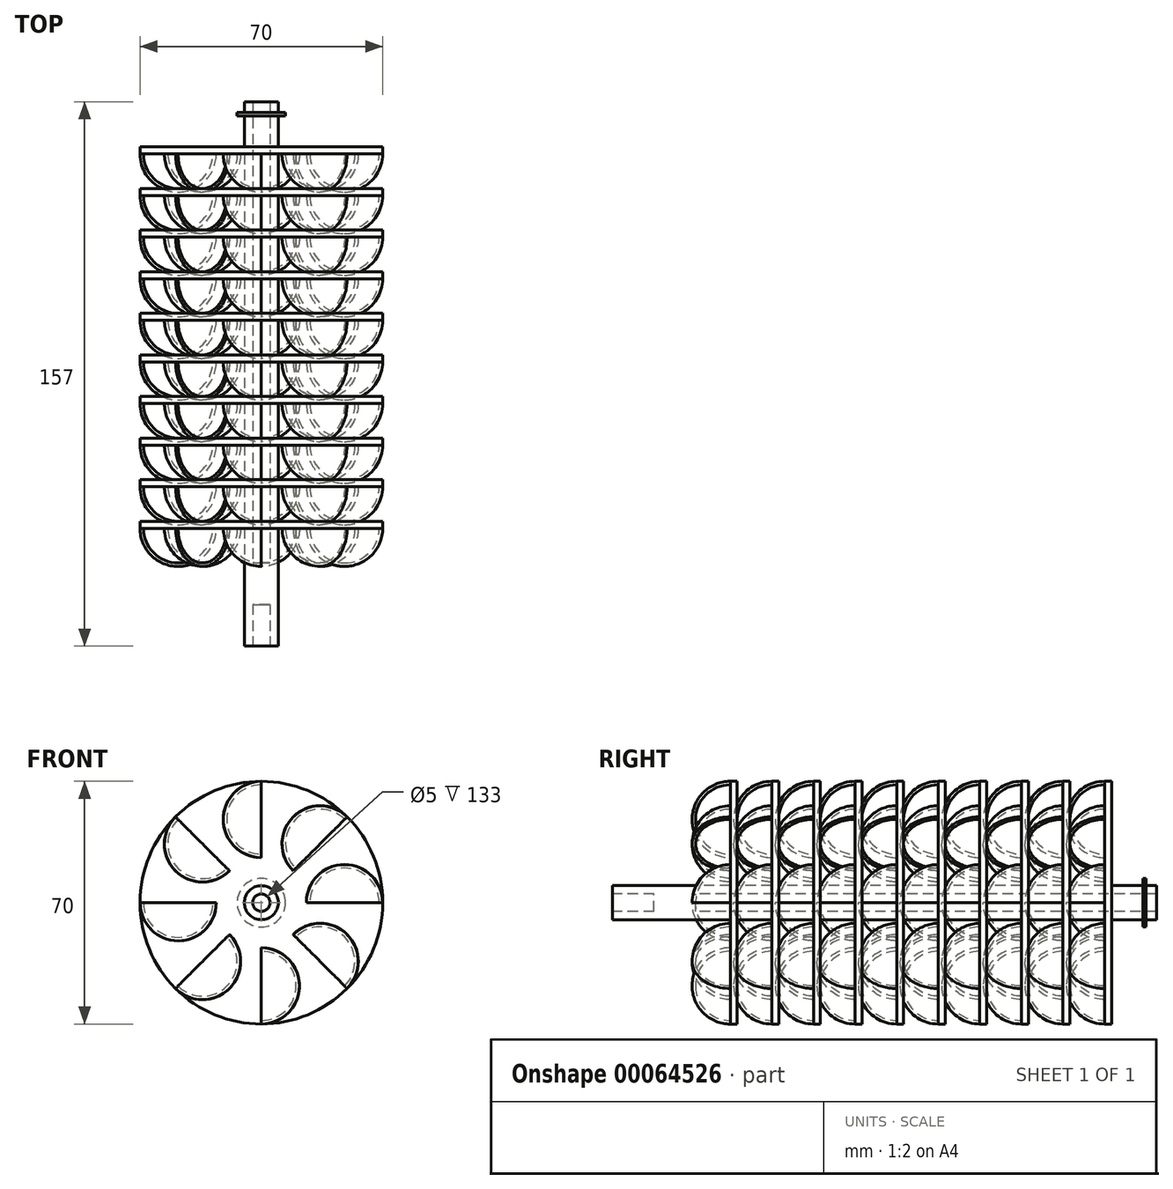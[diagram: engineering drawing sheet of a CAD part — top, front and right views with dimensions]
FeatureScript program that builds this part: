
annotation { "Feature Type Name" : "Feature", "Feature Type Description" : "" }
export const myFeature = defineFeature(function(context is Context, id is Id, definition is map)
    precondition{}
    {
        {
            var Q0;
            Q0=qCreatedBy(makeId("Right.planeOp"),FACE);
            var sketch = newSketch(context, id + "F0", { "sketchPlane" : qUnion([Q0])});
            skArc(sketch, "E0", {"start": v(0, 10) * mm, "mid": v(-7.07, 7.07) * mm, "end": v(-10, 0) * mm});
            skLineSegment(sketch, "E1", {"start": v(-10, 0) * mm, "end": v(0, 0) * mm});
            skLineSegment(sketch, "E2", {"start": v(0, 10) * mm, "end": v(0, 0) * mm});
            skArc(sketch, "E3", {"start": v(0, 11) * mm, "mid": v(-7.78, 7.78) * mm, "end": v(-11, 0) * mm});
            skLineSegment(sketch, "E4", {"start": v(0, 10) * mm, "end": v(0, 11) * mm});
            skLineSegment(sketch, "E5", {"start": v(-11, 0) * mm, "end": v(-10, 0) * mm});
            skSolve(sketch);
        }
        {
            var Q0;
            Q0=makeQuery(id+"F0.imprint","IMPRINT",FACE,{"disambiguationData":[TD([[makeQuery(id+"F0.imprint","IMPRINT",EDGE,{"derivedFrom":sQuery(id+"F0.wireOp",EDGE,"E0")}),-1.0]])]});
            var Q1;
            Q1=sQuery(id+"F0.wireOp",EDGE,"E0");
            var Q2;
            Q2=sQuery(id+"F0.wireOp",EDGE,"E1");
            revolve(context, id + "F1", {"entities" : qUnion([Q0]), "surfaceEntities" : qUnion([Q1]), "axis" : qUnion([Q2]), "revolveType" : RevolveType.TWO_DIRECTIONS, "angle" : 90 * degree, "angleBack" : 270 * degree});
        }
        {
            var Q0;
            Q0=makeQuery(id+"F1.opRevolve","SWEPT_BODY",BODY,{"disambiguationData":[OSD([sQuery(id+"F0.wireOp",EDGE,"E0"),sQuery(id+"F0.wireOp",EDGE,"E3"),sQuery(id+"F0.wireOp",EDGE,"E4"),sQuery(id+"F0.wireOp",EDGE,"E5")])]});
            transform(context, id + "F2", {"entities" : qUnion([Q0]), "transformType" : TransformType.TRANSLATION_3D, "dx" : 24 * mm, "dy" : 0 * mm, "dz" : 0 * mm, "makeCopy" : false});
        }
        {
            var Q0;
            Q0=qCreatedBy(makeId("Right.planeOp"),FACE);
            var sketch = newSketch(context, id + "F3", { "sketchPlane" : qUnion([Q0])});
            skLineSegment(sketch, "E6", {"start": v(-12, 0) * mm, "end": v(0, 0) * mm});
            skLineSegment(sketch, "E7", {"start": v(0, 0) * mm, "end": v(10, 0) * mm});
            skLineSegment(sketch, "E8", {"start": v(0, 0) * mm, "end": v(0, 35) * mm});
            skLineSegment(sketch, "E9.bottom", {"start": v(-2, 0) * mm, "end": v(0, 0) * mm});
            skLineSegment(sketch, "E9.top", {"start": v(-2, 35) * mm, "end": v(0, 35) * mm});
            skLineSegment(sketch, "E9.right", {"start": v(-2, 0) * mm, "end": v(-2, 35) * mm});
            skLineSegment(sketch, "E10", {"start": v(-24, 4.9) * mm, "end": v(0, 4.9) * mm});
            skLineSegment(sketch, "E11", {"start": v(0, 4.9) * mm, "end": v(10, 4.9) * mm});
            skLineSegment(sketch, "E12", {"start": v(-2, 4.9) * mm, "end": v(-2, 0) * mm});
            skLineSegment(sketch, "E13", {"start": v(0, 4.9) * mm, "end": v(0, 0) * mm});
            skLineSegment(sketch, "E14", {"start": v(22, 0) * mm, "end": v(34, 0) * mm});
            skLineSegment(sketch, "E15", {"start": v(34, 0) * mm, "end": v(46, 0) * mm});
            skLineSegment(sketch, "E16", {"start": v(-12, 0) * mm, "end": v(-24, 0) * mm});
            skLineSegment(sketch, "E17", {"start": v(-24, 0) * mm, "end": v(-36, 0) * mm});
            skLineSegment(sketch, "E18", {"start": v(-36, 0) * mm, "end": v(-48, 0) * mm});
            skLineSegment(sketch, "E19", {"start": v(10, 0) * mm, "end": v(22, 0) * mm});
            skLineSegment(sketch, "E20", {"start": v(46, 0) * mm, "end": v(58, 0) * mm});
            skLineSegment(sketch, "E21", {"start": v(-24, 4.9) * mm, "end": v(-24, 4.9) * mm});
            skLineSegment(sketch, "E22", {"start": v(10, 4.9) * mm, "end": v(22, 4.9) * mm});
            skLineSegment(sketch, "E23", {"start": v(-24, 4.9) * mm, "end": v(-36, 4.9) * mm});
            skLineSegment(sketch, "E24", {"start": v(-36, 0) * mm, "end": v(-36, 4.9) * mm});
            skLineSegment(sketch, "E25", {"start": v(58, 0) * mm, "end": v(73, 0) * mm});
            skLineSegment(sketch, "E26", {"start": v(73, 0) * mm, "end": v(85, 0) * mm});
            skLineSegment(sketch, "E27", {"start": v(-48, 0) * mm, "end": v(-60, 0) * mm});
            skLineSegment(sketch, "E28", {"start": v(-36, 0) * mm, "end": v(-36, 2.5) * mm});
            skLineSegment(sketch, "E29", {"start": v(-36, 2.5) * mm, "end": v(22, 2.5) * mm});
            skLineSegment(sketch, "E30", {"start": v(-36, 0) * mm, "end": v(-38, 0) * mm});
            skLineSegment(sketch, "E31", {"start": v(10, 4.9) * mm, "end": v(10, 0) * mm});
            skLineSegment(sketch, "E32", {"start": v(10, 0) * mm, "end": v(10, 35) * mm});
            skLineSegment(sketch, "E33", {"start": v(10, 35) * mm, "end": v(12, 35) * mm});
            skLineSegment(sketch, "E34", {"start": v(12, 35) * mm, "end": v(12, 0) * mm});
            skLineSegment(sketch, "E35", {"start": v(22, 0) * mm, "end": v(22, 35) * mm});
            skLineSegment(sketch, "E36", {"start": v(22, 35) * mm, "end": v(24, 35) * mm});
            skLineSegment(sketch, "E37", {"start": v(24, 35) * mm, "end": v(24, 0) * mm});
            skLineSegment(sketch, "E38", {"start": v(34, 0) * mm, "end": v(34, 35) * mm});
            skLineSegment(sketch, "E39", {"start": v(34, 35) * mm, "end": v(36, 35) * mm});
            skLineSegment(sketch, "E40", {"start": v(36, 35) * mm, "end": v(36, 0) * mm});
            skLineSegment(sketch, "E41", {"start": v(46, 0) * mm, "end": v(46, 35) * mm});
            skLineSegment(sketch, "E42", {"start": v(46, 35) * mm, "end": v(48, 35) * mm});
            skLineSegment(sketch, "E43", {"start": v(48, 35) * mm, "end": v(48, 0) * mm});
            skLineSegment(sketch, "E44", {"start": v(58, 0) * mm, "end": v(58, 35) * mm});
            skLineSegment(sketch, "E45", {"start": v(58, 35) * mm, "end": v(60, 35) * mm});
            skLineSegment(sketch, "E46", {"start": v(60, 35) * mm, "end": v(60, 0) * mm});
            skLineSegment(sketch, "E47", {"start": v(22, 4.9) * mm, "end": v(34, 4.9) * mm});
            skLineSegment(sketch, "E48", {"start": v(34, 4.9) * mm, "end": v(46, 4.9) * mm});
            skLineSegment(sketch, "E49", {"start": v(46, 4.9) * mm, "end": v(58, 4.9) * mm});
            skLineSegment(sketch, "E50", {"start": v(58, 4.9) * mm, "end": v(73, 4.9) * mm});
            skLineSegment(sketch, "E51", {"start": v(73, 4.9) * mm, "end": v(73, 0) * mm});
            skLineSegment(sketch, "E52", {"start": v(22, 2.5) * mm, "end": v(48, 2.5) * mm});
            skLineSegment(sketch, "E53", {"start": v(48, 2.5) * mm, "end": v(73, 2.5) * mm});
            skLineSegment(sketch, "E54", {"start": v(-12, 0) * mm, "end": v(-12, 35) * mm});
            skLineSegment(sketch, "E55", {"start": v(-12, 35) * mm, "end": v(-14, 35) * mm});
            skLineSegment(sketch, "E56", {"start": v(-14, 35) * mm, "end": v(-14, 0) * mm});
            skLineSegment(sketch, "E57", {"start": v(-24, 0) * mm, "end": v(-24, 35) * mm});
            skLineSegment(sketch, "E58", {"start": v(-24, 35) * mm, "end": v(-26, 35) * mm});
            skLineSegment(sketch, "E59", {"start": v(-26, 35) * mm, "end": v(-26, 0) * mm});
            skLineSegment(sketch, "E60", {"start": v(-36, 0) * mm, "end": v(-36, 35) * mm});
            skLineSegment(sketch, "E61", {"start": v(-36, 35) * mm, "end": v(-38, 35) * mm});
            skLineSegment(sketch, "E62", {"start": v(-38, 35) * mm, "end": v(-38, 0) * mm});
            skLineSegment(sketch, "E63", {"start": v(-48, 0) * mm, "end": v(-48, 35) * mm});
            skLineSegment(sketch, "E64", {"start": v(-48, 35) * mm, "end": v(-50, 35) * mm});
            skLineSegment(sketch, "E65", {"start": v(-50, 35) * mm, "end": v(-50, 0) * mm});
            skLineSegment(sketch, "E66", {"start": v(-36, 4.9) * mm, "end": v(-50, 4.9) * mm});
            skLineSegment(sketch, "E67", {"start": v(-50, 4.9) * mm, "end": v(-60, 4.9) * mm});
            skLineSegment(sketch, "E68", {"start": v(-60, 4.9) * mm, "end": v(-60, 0) * mm});
            skLineSegment(sketch, "E69", {"start": v(-36, 2.5) * mm, "end": v(-60, 2.5) * mm});
            skLineSegment(sketch, "E70", {"start": v(-60, 0) * mm, "end": v(-60, 2.5) * mm});
            skLineSegment(sketch, "E71", {"start": v(-2, 4.9) * mm, "end": v(0, 4.9) * mm});
            skLineSegment(sketch, "E72", {"start": v(0, 0) * mm, "end": v(-2, 0) * mm});
            skLineSegment(sketch, "E73", {"start": v(10, 0) * mm, "end": v(-2, 0) * mm});
            skLineSegment(sketch, "E74", {"start": v(10, 4.9) * mm, "end": v(-2, 4.9) * mm});
            skLineSegment(sketch, "E75", {"start": v(22, 2.5) * mm, "end": v(12, 2.5) * mm});
            skLineSegment(sketch, "E76", {"start": v(-2, 4.9) * mm, "end": v(10, 4.9) * mm});
            skLineSegment(sketch, "E77", {"start": v(-60, 4.9) * mm, "end": v(-72, 4.9) * mm});
            skLineSegment(sketch, "E78", {"start": v(-72, 4.9) * mm, "end": v(-72, 0) * mm});
            skLineSegment(sketch, "E79", {"start": v(-72, 0) * mm, "end": v(-60, 0) * mm});
            skLineSegment(sketch, "E80", {"start": v(-72, 4.9) * mm, "end": v(-84, 4.9) * mm});
            skLineSegment(sketch, "E81", {"start": v(-84, 4.9) * mm, "end": v(-84, 0) * mm});
            skLineSegment(sketch, "E82", {"start": v(-84, 0) * mm, "end": v(-72, 0) * mm});
            skLineSegment(sketch, "E83", {"start": v(-60, 2.5) * mm, "end": v(-84, 2.5) * mm});
            skLineSegment(sketch, "E84", {"start": v(-84, 0) * mm, "end": v(-84, 2.5) * mm});
            skLineSegment(sketch, "E85", {"start": v(70, 0) * mm, "end": v(70, 7) * mm});
            skLineSegment(sketch, "E86", {"start": v(70, 7) * mm, "end": v(69, 7) * mm});
            skLineSegment(sketch, "E87", {"start": v(69, 0) * mm, "end": v(69, 7) * mm});
            skSolve(sketch);
        }
        {
            var Q0;
            Q0=makeQuery(id+"F3.imprint","IMPRINT",FACE,{"disambiguationData":[TD([[makeQuery(id+"F3.imprint","IMPRINT",EDGE,{"derivedFrom":sQuery(id+"F3.wireOp",EDGE,"E6")}),-1.0]])]});
            var Q1;
            Q1=makeQuery(id+"F3.imprint","IMPRINT",FACE,{"disambiguationData":[TD([[makeQuery(id+"F3.imprint","IMPRINT",EDGE,{"derivedFrom":sQuery(id+"F3.wireOp",EDGE,"E7")}),-1.0]])]});
            var Q2;
            Q2=makeQuery(id+"F3.imprint","IMPRINT",FACE,{"disambiguationData":[TD([[makeQuery(id+"F3.imprint","IMPRINT",EDGE,{"derivedFrom":sQuery(id+"F3.wireOp",EDGE,"E11")}),1.0]])]});
            var Q3;
            Q3=makeQuery(id+"F3.imprint","IMPRINT",FACE,{"disambiguationData":[TD([[makeQuery(id+"F3.imprint","IMPRINT",EDGE,{"derivedFrom":sQuery(id+"F3.wireOp",EDGE,"HCRJPAIn-l69N-Ecoj-YLD3-3IPwDvo4FcGq")}),-1.0]])]});
            var Q4;
            Q4=makeQuery(id+"F3.imprint","IMPRINT",FACE,{"disambiguationData":[TD([[makeQuery(id+"F3.imprint","IMPRINT",EDGE,{"derivedFrom":sQuery(id+"F3.wireOp",EDGE,"tsCGz1Qc-Ed8h-9qHw-DWUl-nttLdNUFEeCr")}),-1.0]])]});
            var Q5;
            Q5=makeQuery(id+"F3.imprint","IMPRINT",FACE,{"disambiguationData":[TD([[makeQuery(id+"F3.imprint","IMPRINT",EDGE,{"derivedFrom":sQuery(id+"F3.wireOp",EDGE,"E17")}),1.0]])]});
            var Q6;
            Q6=makeQuery(id+"F3.imprint","IMPRINT",FACE,{"disambiguationData":[TD([[makeQuery(id+"F3.imprint","IMPRINT",EDGE,{"derivedFrom":sQuery(id+"F3.wireOp",EDGE,"E14")}),-1.0]])]});
            var Q7;
            {var subQ0=sQuery(id+"F3.wireOp",EDGE,"E21");Q7=makeQuery(id+"F3.imprint","IMPRINT",FACE,{"disambiguationData":[TD([[makeQuery(id+"F3.imprint","IMPRINT",EDGE,{"derivedFrom":subQ0}),1.0]])]});}
            var Q8;
            {var subQ0=sQuery(id+"F3.wireOp",EDGE,"E67");Q8=makeQuery(id+"F3.imprint","IMPRINT",FACE,{"disambiguationData":[TD([[makeQuery(id+"F3.imprint","IMPRINT",EDGE,{"derivedFrom":subQ0}),1.0]])]});}
            var Q9;
            {var subQ0=sQuery(id+"F3.wireOp",EDGE,"E66");var subQ1=sQuery(id+"F3.wireOp",EDGE,"E63");var subQ2=makeQuery(id+"F3.imprint","INTERSECT",VERTEX,{"derivedFrom":[subQ1,subQ0]});Q9=makeQuery(id+"F3.imprint","IMPRINT",FACE,{"disambiguationData":[TD([[makeQuery(id+"F3.imprint","IMPRINT",EDGE,{"disambiguationData":[TD([[subQ2,1.0]])],"derivedFrom":subQ1}),1.0]])]});}
            var Q10;
            {var subQ0=sQuery(id+"F3.wireOp",EDGE,"E64");Q10=makeQuery(id+"F3.imprint","IMPRINT",FACE,{"disambiguationData":[TD([[makeQuery(id+"F3.imprint","IMPRINT",EDGE,{"derivedFrom":subQ0}),1.0]])]});}
            var Q11;
            {var subQ0=sQuery(id+"F3.wireOp",EDGE,"E66");var subQ1=sQuery(id+"F3.wireOp",EDGE,"E62");var subQ2=makeQuery(id+"F3.imprint","INTERSECT",VERTEX,{"derivedFrom":[subQ1,subQ0]});Q11=makeQuery(id+"F3.imprint","IMPRINT",FACE,{"disambiguationData":[TD([[makeQuery(id+"F3.imprint","IMPRINT",EDGE,{"disambiguationData":[TD([[subQ2,-1.0]])],"derivedFrom":subQ1}),-1.0]])]});}
            var Q12;
            {var subQ0=sQuery(id+"F3.wireOp",EDGE,"E66");var subQ5=sQuery(id+"F3.wireOp",EDGE,"E62");var subQ6=makeQuery(id+"F3.imprint","INTERSECT",VERTEX,{"derivedFrom":[subQ5,subQ0]});Q12=makeQuery(id+"F3.imprint","IMPRINT",FACE,{"disambiguationData":[TD([[makeQuery(id+"F3.imprint","IMPRINT",EDGE,{"disambiguationData":[TD([[subQ6,-1.0]])],"derivedFrom":subQ5}),1.0]])]});}
            var Q13;
            {var subQ3=sQuery(id+"F3.wireOp",EDGE,"E61");Q13=makeQuery(id+"F3.imprint","IMPRINT",FACE,{"disambiguationData":[TD([[makeQuery(id+"F3.imprint","IMPRINT",EDGE,{"derivedFrom":subQ3}),1.0]])]});}
            var Q14;
            {var subQ1=sQuery(id+"F3.wireOp",EDGE,"E23");var subQ3=sQuery(id+"F3.wireOp",EDGE,"E59");var subQ4=makeQuery(id+"F3.imprint","INTERSECT",VERTEX,{"derivedFrom":[subQ1,subQ3]});Q14=makeQuery(id+"F3.imprint","IMPRINT",FACE,{"disambiguationData":[TD([[makeQuery(id+"F3.imprint","IMPRINT",EDGE,{"disambiguationData":[TD([[subQ4,-1.0]])],"derivedFrom":subQ3}),-1.0]])]});}
            var Q15;
            {var subQ1=sQuery(id+"F3.wireOp",EDGE,"E23");var subQ7=makeQuery(id+"F3.imprint","IMPRINT",VERTEX,{"derivedFrom":subQ1});Q15=makeQuery(id+"F3.imprint","IMPRINT",FACE,{"disambiguationData":[TD([[makeQuery(id+"F3.imprint","IMPRINT",EDGE,{"disambiguationData":[TD([[subQ7,-1.0]])],"derivedFrom":subQ1}),1.0]])]});}
            var Q16;
            {var subQ3=sQuery(id+"F3.wireOp",EDGE,"E58");Q16=makeQuery(id+"F3.imprint","IMPRINT",FACE,{"disambiguationData":[TD([[makeQuery(id+"F3.imprint","IMPRINT",EDGE,{"derivedFrom":subQ3}),1.0]])]});}
            var Q17;
            {var subQ0=sQuery(id+"F3.wireOp",EDGE,"E57");var subQ5=sQuery(id+"F3.wireOp",EDGE,"E29");var subQ6=makeQuery(id+"F3.imprint","INTERSECT",VERTEX,{"derivedFrom":[subQ5,subQ0]});Q17=makeQuery(id+"F3.imprint","IMPRINT",FACE,{"disambiguationData":[TD([[makeQuery(id+"F3.imprint","IMPRINT",EDGE,{"disambiguationData":[TD([[subQ6,-1.0]])],"derivedFrom":subQ5}),1.0]])]});}
            var Q18;
            {var subQ0=sQuery(id+"F3.wireOp",EDGE,"E56");var subQ1=sQuery(id+"F3.wireOp",EDGE,"E10");var subQ2=makeQuery(id+"F3.imprint","INTERSECT",VERTEX,{"derivedFrom":[subQ1,subQ0]});Q18=makeQuery(id+"F3.imprint","IMPRINT",FACE,{"disambiguationData":[TD([[makeQuery(id+"F3.imprint","IMPRINT",EDGE,{"disambiguationData":[TD([[subQ2,-1.0]])],"derivedFrom":subQ1}),-1.0]])]});}
            var Q19;
            {var subQ5=sQuery(id+"F3.wireOp",EDGE,"E55");Q19=makeQuery(id+"F3.imprint","IMPRINT",FACE,{"disambiguationData":[TD([[makeQuery(id+"F3.imprint","IMPRINT",EDGE,{"derivedFrom":subQ5}),1.0]])]});}
            var Q20;
            {var subQ0=sQuery(id+"F3.wireOp",EDGE,"E12");var subQ5=sQuery(id+"F3.wireOp",EDGE,"E29");var subQ6=makeQuery(id+"F3.imprint","INTERSECT",VERTEX,{"derivedFrom":[subQ0,subQ5]});Q20=makeQuery(id+"F3.imprint","IMPRINT",FACE,{"disambiguationData":[TD([[makeQuery(id+"F3.imprint","IMPRINT",EDGE,{"disambiguationData":[TD([[subQ6,1.0]])],"derivedFrom":subQ5}),1.0]])]});}
            var Q21;
            {var subQ0=sQuery(id+"F3.wireOp",EDGE,"E50");var subQ1=sQuery(id+"F3.wireOp",EDGE,"E46");var subQ2=makeQuery(id+"F3.imprint","INTERSECT",VERTEX,{"derivedFrom":[subQ1,subQ0]});Q21=makeQuery(id+"F3.imprint","IMPRINT",FACE,{"disambiguationData":[TD([[makeQuery(id+"F3.imprint","IMPRINT",EDGE,{"disambiguationData":[TD([[subQ2,-1.0]])],"derivedFrom":subQ1}),1.0]])]});}
            var Q22;
            {var subQ0=sQuery(id+"F3.wireOp",EDGE,"E50");var subQ5=sQuery(id+"F3.wireOp",EDGE,"E46");var subQ7=makeQuery(id+"F3.imprint","INTERSECT",VERTEX,{"derivedFrom":[subQ5,subQ0]});Q22=makeQuery(id+"F3.imprint","IMPRINT",FACE,{"disambiguationData":[TD([[makeQuery(id+"F3.imprint","IMPRINT",EDGE,{"disambiguationData":[TD([[subQ7,-1.0]])],"derivedFrom":subQ5}),-1.0]])]});}
            var Q23;
            {var subQ0=sQuery(id+"F3.wireOp",EDGE,"E45");Q23=makeQuery(id+"F3.imprint","IMPRINT",FACE,{"disambiguationData":[TD([[makeQuery(id+"F3.imprint","IMPRINT",EDGE,{"derivedFrom":subQ0}),-1.0]])]});}
            var Q24;
            {var subQ1=sQuery(id+"F3.wireOp",EDGE,"E43");var subQ3=sQuery(id+"F3.wireOp",EDGE,"E49");var subQ4=makeQuery(id+"F3.imprint","INTERSECT",VERTEX,{"derivedFrom":[subQ1,subQ3]});Q24=makeQuery(id+"F3.imprint","IMPRINT",FACE,{"disambiguationData":[TD([[makeQuery(id+"F3.imprint","IMPRINT",EDGE,{"disambiguationData":[TD([[subQ4,-1.0]])],"derivedFrom":subQ1}),1.0]])]});}
            var Q25;
            {var subQ1=sQuery(id+"F3.wireOp",EDGE,"E41");var subQ3=sQuery(id+"F3.wireOp",EDGE,"E52");var subQ4=makeQuery(id+"F3.imprint","INTERSECT",VERTEX,{"derivedFrom":[subQ1,subQ3]});Q25=makeQuery(id+"F3.imprint","IMPRINT",FACE,{"disambiguationData":[TD([[makeQuery(id+"F3.imprint","IMPRINT",EDGE,{"disambiguationData":[TD([[subQ4,-1.0]])],"derivedFrom":subQ1}),-1.0]])]});}
            var Q26;
            {var subQ0=sQuery(id+"F3.wireOp",EDGE,"E42");Q26=makeQuery(id+"F3.imprint","IMPRINT",FACE,{"disambiguationData":[TD([[makeQuery(id+"F3.imprint","IMPRINT",EDGE,{"derivedFrom":subQ0}),-1.0]])]});}
            var Q27;
            {var subQ0=sQuery(id+"F3.wireOp",EDGE,"E48");var subQ1=sQuery(id+"F3.wireOp",EDGE,"E40");var subQ2=makeQuery(id+"F3.imprint","INTERSECT",VERTEX,{"derivedFrom":[subQ1,subQ0]});Q27=makeQuery(id+"F3.imprint","IMPRINT",FACE,{"disambiguationData":[TD([[makeQuery(id+"F3.imprint","IMPRINT",EDGE,{"disambiguationData":[TD([[subQ2,-1.0]])],"derivedFrom":subQ1}),1.0]])]});}
            var Q28;
            {var subQ0=sQuery(id+"F3.wireOp",EDGE,"E48");var subQ5=sQuery(id+"F3.wireOp",EDGE,"E40");var subQ6=makeQuery(id+"F3.imprint","INTERSECT",VERTEX,{"derivedFrom":[subQ5,subQ0]});Q28=makeQuery(id+"F3.imprint","IMPRINT",FACE,{"disambiguationData":[TD([[makeQuery(id+"F3.imprint","IMPRINT",EDGE,{"disambiguationData":[TD([[subQ6,-1.0]])],"derivedFrom":subQ5}),-1.0]])]});}
            var Q29;
            {var subQ0=sQuery(id+"F3.wireOp",EDGE,"E39");Q29=makeQuery(id+"F3.imprint","IMPRINT",FACE,{"disambiguationData":[TD([[makeQuery(id+"F3.imprint","IMPRINT",EDGE,{"derivedFrom":subQ0}),-1.0]])]});}
            var Q30;
            {var subQ0=sQuery(id+"F3.wireOp",EDGE,"E47");var subQ1=sQuery(id+"F3.wireOp",EDGE,"E37");var subQ2=makeQuery(id+"F3.imprint","INTERSECT",VERTEX,{"derivedFrom":[subQ1,subQ0]});Q30=makeQuery(id+"F3.imprint","IMPRINT",FACE,{"disambiguationData":[TD([[makeQuery(id+"F3.imprint","IMPRINT",EDGE,{"disambiguationData":[TD([[subQ2,-1.0]])],"derivedFrom":subQ1}),1.0]])]});}
            var Q31;
            {var subQ0=sQuery(id+"F3.wireOp",EDGE,"E47");var subQ5=sQuery(id+"F3.wireOp",EDGE,"E37");var subQ7=makeQuery(id+"F3.imprint","INTERSECT",VERTEX,{"derivedFrom":[subQ5,subQ0]});Q31=makeQuery(id+"F3.imprint","IMPRINT",FACE,{"disambiguationData":[TD([[makeQuery(id+"F3.imprint","IMPRINT",EDGE,{"disambiguationData":[TD([[subQ7,-1.0]])],"derivedFrom":subQ5}),-1.0]])]});}
            var Q32;
            {var subQ3=sQuery(id+"F3.wireOp",EDGE,"E36");Q32=makeQuery(id+"F3.imprint","IMPRINT",FACE,{"disambiguationData":[TD([[makeQuery(id+"F3.imprint","IMPRINT",EDGE,{"derivedFrom":subQ3}),-1.0]])]});}
            var Q33;
            {var subQ1=sQuery(id+"F3.wireOp",EDGE,"E22");var subQ3=sQuery(id+"F3.wireOp",EDGE,"E34");var subQ4=makeQuery(id+"F3.imprint","INTERSECT",VERTEX,{"derivedFrom":[subQ1,subQ3]});Q33=makeQuery(id+"F3.imprint","IMPRINT",FACE,{"disambiguationData":[TD([[makeQuery(id+"F3.imprint","IMPRINT",EDGE,{"disambiguationData":[TD([[subQ4,-1.0]])],"derivedFrom":subQ3}),1.0]])]});}
            var Q34;
            {var subQ0=sQuery(id+"F3.wireOp",EDGE,"E32");var subQ5=sQuery(id+"F3.wireOp",EDGE,"E29");var subQ6=makeQuery(id+"F3.imprint","INTERSECT",VERTEX,{"derivedFrom":[subQ5,subQ0]});Q34=makeQuery(id+"F3.imprint","IMPRINT",FACE,{"disambiguationData":[TD([[makeQuery(id+"F3.imprint","IMPRINT",EDGE,{"disambiguationData":[TD([[subQ6,-1.0]])],"derivedFrom":subQ5}),1.0]])]});}
            var Q35;
            {var subQ5=sQuery(id+"F3.wireOp",EDGE,"E33");Q35=makeQuery(id+"F3.imprint","IMPRINT",FACE,{"disambiguationData":[TD([[makeQuery(id+"F3.imprint","IMPRINT",EDGE,{"derivedFrom":subQ5}),-1.0]])]});}
            var Q36;
            {var subQ0=sQuery(id+"F3.wireOp",EDGE,"E11");Q36=makeQuery(id+"F3.imprint","IMPRINT",FACE,{"disambiguationData":[TD([[makeQuery(id+"F3.imprint","IMPRINT",EDGE,{"derivedFrom":subQ0}),-1.0]])]});}
            var Q37;
            {var subQ0=sQuery(id+"F3.wireOp",EDGE,"E71");Q37=makeQuery(id+"F3.imprint","IMPRINT",FACE,{"disambiguationData":[TD([[makeQuery(id+"F3.imprint","IMPRINT",EDGE,{"derivedFrom":subQ0}),-1.0]])]});}
            var Q38;
            {var subQ1=sQuery(id+"F3.wireOp",EDGE,"E13");var subQ3=sQuery(id+"F3.wireOp",EDGE,"E29");var subQ4=makeQuery(id+"F3.imprint","INTERSECT",VERTEX,{"derivedFrom":[subQ1,subQ3]});Q38=makeQuery(id+"F3.imprint","IMPRINT",FACE,{"disambiguationData":[TD([[makeQuery(id+"F3.imprint","IMPRINT",EDGE,{"disambiguationData":[TD([[subQ4,-1.0]])],"derivedFrom":subQ3}),1.0]])]});}
            var Q39;
            {var subQ1=sQuery(id+"F3.wireOp",EDGE,"E12");var subQ3=sQuery(id+"F3.wireOp",EDGE,"E29");var subQ4=makeQuery(id+"F3.imprint","INTERSECT",VERTEX,{"derivedFrom":[subQ1,subQ3]});Q39=makeQuery(id+"F3.imprint","IMPRINT",FACE,{"disambiguationData":[TD([[makeQuery(id+"F3.imprint","IMPRINT",EDGE,{"disambiguationData":[TD([[subQ4,-1.0]])],"derivedFrom":subQ3}),1.0]])]});}
            var Q40;
            Q40=makeQuery(id+"F3.imprint","IMPRINT",FACE,{"disambiguationData":[TD([[makeQuery(id+"F3.imprint","IMPRINT",EDGE,{"derivedFrom":sQuery(id+"F3.wireOp",EDGE,"E9.top")}),-1.0]])]});
            var Q41;
            {var subQ0=sQuery(id+"F3.wireOp",EDGE,"E68");Q41=makeQuery(id+"F3.imprint","IMPRINT",FACE,{"disambiguationData":[TD([[makeQuery(id+"F3.imprint","IMPRINT",EDGE,{"derivedFrom":subQ0}),-1.0]])]});}
            var Q42;
            {var subQ0=sQuery(id+"F3.wireOp",EDGE,"E80");Q42=makeQuery(id+"F3.imprint","IMPRINT",FACE,{"disambiguationData":[TD([[makeQuery(id+"F3.imprint","IMPRINT",EDGE,{"derivedFrom":subQ0}),1.0]])]});}
            var Q43;
            {var subQ0=sQuery(id+"F3.wireOp",EDGE,"E51");var subQ1=sQuery(id+"F3.wireOp",EDGE,"E50");var subQ2=makeQuery(id+"F3.imprint","INTERSECT",VERTEX,{"derivedFrom":[subQ1,subQ0]});Q43=makeQuery(id+"F3.imprint","IMPRINT",FACE,{"disambiguationData":[TD([[makeQuery(id+"F3.imprint","IMPRINT",EDGE,{"disambiguationData":[TD([[subQ2,1.0]])],"derivedFrom":subQ1}),-1.0]])]});}
            var Q44;
            {var subQ0=sQuery(id+"F3.wireOp",EDGE,"E87");var subQ1=sQuery(id+"F3.wireOp",EDGE,"E50");var subQ2=makeQuery(id+"F3.imprint","INTERSECT",VERTEX,{"derivedFrom":[subQ1,subQ0]});Q44=makeQuery(id+"F3.imprint","IMPRINT",FACE,{"disambiguationData":[TD([[makeQuery(id+"F3.imprint","IMPRINT",EDGE,{"disambiguationData":[TD([[subQ2,-1.0]])],"derivedFrom":subQ1}),-1.0]])]});}
            var Q45;
            {var subQ5=sQuery(id+"F3.wireOp",EDGE,"E86");Q45=makeQuery(id+"F3.imprint","IMPRINT",FACE,{"disambiguationData":[TD([[makeQuery(id+"F3.imprint","IMPRINT",EDGE,{"derivedFrom":subQ5}),1.0]])]});}
            var Q46;
            Q46=sQuery(id+"F3.wireOp",EDGE,"E6");
            revolve(context, id + "F4", {"entities" : qUnion([Q0, Q1, Q2, Q3, Q4, Q5, Q6, Q7, Q8, Q9, Q10, Q11, Q12, Q13, Q14, Q15, Q16, Q17, Q18, Q19, Q20, Q21, Q22, Q23, Q24, Q25, Q26, Q27, Q28, Q29, Q30, Q31, Q32, Q33, Q34, Q35, Q36, Q37, Q38, Q39, Q40, Q41, Q42, Q43, Q44, Q45]), "axis" : qUnion([Q46]), "revolveType" : RevolveType.FULL});
        }
        {
            var Q0;
            Q0=makeQuery(id+"F1.opRevolve","SWEPT_BODY",BODY,{"disambiguationData":[OSD([sQuery(id+"F0.wireOp",EDGE,"E0"),sQuery(id+"F0.wireOp",EDGE,"E3"),sQuery(id+"F0.wireOp",EDGE,"E4"),sQuery(id+"F0.wireOp",EDGE,"E5")])]});
            var Q1;
            Q1=sQuery(id+"F3.wireOp",EDGE,"E6");
            transform(context, id + "F5", {"entities" : qUnion([Q0]), "transformType" : TransformType.ROTATION, "transformAxis" : qUnion([Q1]), "angle" : 90 * degree, "makeCopy" : true});
        }
        {
            var Q0;
            Q0=makeQuery(id+"F1.opRevolve","SWEPT_BODY",BODY,{"disambiguationData":[OSD([sQuery(id+"F0.wireOp",EDGE,"E0"),sQuery(id+"F0.wireOp",EDGE,"E3"),sQuery(id+"F0.wireOp",EDGE,"E4"),sQuery(id+"F0.wireOp",EDGE,"E5")])]});
            var Q1;
            Q1=makeQuery(id+"F5.opPattern","COPY",BODY,{"derivedFrom":makeQuery(id+"F1.opRevolve","SWEPT_BODY",BODY,{"disambiguationData":[OSD([sQuery(id+"F0.wireOp",EDGE,"E0"),sQuery(id+"F0.wireOp",EDGE,"E3"),sQuery(id+"F0.wireOp",EDGE,"E4"),sQuery(id+"F0.wireOp",EDGE,"E5")])]}),"instanceName":"1"});
            var Q2;
            Q2=sQuery(id+"F3.wireOp",EDGE,"E7");
            transform(context, id + "F6", {"entities" : qUnion([Q0, Q1]), "transformType" : TransformType.ROTATION, "transformAxis" : qUnion([Q2]), "angle" : 180 * degree, "makeCopy" : true});
        }
        {
            var Q0;
            Q0=makeQuery(id+"F1.opRevolve","SWEPT_BODY",BODY,{"disambiguationData":[OSD([sQuery(id+"F0.wireOp",EDGE,"E0"),sQuery(id+"F0.wireOp",EDGE,"E3"),sQuery(id+"F0.wireOp",EDGE,"E4"),sQuery(id+"F0.wireOp",EDGE,"E5")])]});
            var Q1;
            Q1=makeQuery(id+"F6.opPattern","COPY",BODY,{"derivedFrom":makeQuery(id+"F5.opPattern","COPY",BODY,{"derivedFrom":makeQuery(id+"F1.opRevolve","SWEPT_BODY",BODY,{"disambiguationData":[OSD([sQuery(id+"F0.wireOp",EDGE,"E0"),sQuery(id+"F0.wireOp",EDGE,"E3"),sQuery(id+"F0.wireOp",EDGE,"E4"),sQuery(id+"F0.wireOp",EDGE,"E5")])]}),"instanceName":"1"}),"instanceName":"1"});
            var Q2;
            Q2=makeQuery(id+"F6.opPattern","COPY",BODY,{"derivedFrom":makeQuery(id+"F1.opRevolve","SWEPT_BODY",BODY,{"disambiguationData":[OSD([sQuery(id+"F0.wireOp",EDGE,"E0"),sQuery(id+"F0.wireOp",EDGE,"E3"),sQuery(id+"F0.wireOp",EDGE,"E4"),sQuery(id+"F0.wireOp",EDGE,"E5")])]}),"instanceName":"1"});
            var Q3;
            Q3=makeQuery(id+"F5.opPattern","COPY",BODY,{"derivedFrom":makeQuery(id+"F1.opRevolve","SWEPT_BODY",BODY,{"disambiguationData":[OSD([sQuery(id+"F0.wireOp",EDGE,"E0"),sQuery(id+"F0.wireOp",EDGE,"E3"),sQuery(id+"F0.wireOp",EDGE,"E4"),sQuery(id+"F0.wireOp",EDGE,"E5")])]}),"instanceName":"1"});
            var Q4;
            Q4=sQuery(id+"F3.wireOp",EDGE,"E26");
            transform(context, id + "F7", {"entities" : qUnion([Q0, Q1, Q2, Q3]), "transformType" : TransformType.ROTATION, "transformAxis" : qUnion([Q4]), "angle" : 45 * degree, "makeCopy" : true});
        }
        {
            var Q0;
            Q0=makeQuery(id+"F1.opRevolve","SWEPT_BODY",BODY,{"disambiguationData":[OSD([sQuery(id+"F0.wireOp",EDGE,"E0"),sQuery(id+"F0.wireOp",EDGE,"E3"),sQuery(id+"F0.wireOp",EDGE,"E4"),sQuery(id+"F0.wireOp",EDGE,"E5")])]});
            var Q1;
            Q1=makeQuery(id+"F7.opPattern","COPY",BODY,{"derivedFrom":makeQuery(id+"F1.opRevolve","SWEPT_BODY",BODY,{"disambiguationData":[OSD([sQuery(id+"F0.wireOp",EDGE,"E0"),sQuery(id+"F0.wireOp",EDGE,"E3"),sQuery(id+"F0.wireOp",EDGE,"E4"),sQuery(id+"F0.wireOp",EDGE,"E5")])]}),"instanceName":"1"});
            var Q2;
            Q2=makeQuery(id+"F5.opPattern","COPY",BODY,{"derivedFrom":makeQuery(id+"F1.opRevolve","SWEPT_BODY",BODY,{"disambiguationData":[OSD([sQuery(id+"F0.wireOp",EDGE,"E0"),sQuery(id+"F0.wireOp",EDGE,"E3"),sQuery(id+"F0.wireOp",EDGE,"E4"),sQuery(id+"F0.wireOp",EDGE,"E5")])]}),"instanceName":"1"});
            var Q3;
            Q3=makeQuery(id+"F7.opPattern","COPY",BODY,{"derivedFrom":makeQuery(id+"F5.opPattern","COPY",BODY,{"derivedFrom":makeQuery(id+"F1.opRevolve","SWEPT_BODY",BODY,{"disambiguationData":[OSD([sQuery(id+"F0.wireOp",EDGE,"E0"),sQuery(id+"F0.wireOp",EDGE,"E3"),sQuery(id+"F0.wireOp",EDGE,"E4"),sQuery(id+"F0.wireOp",EDGE,"E5")])]}),"instanceName":"1"}),"instanceName":"1"});
            var Q4;
            Q4=makeQuery(id+"F6.opPattern","COPY",BODY,{"derivedFrom":makeQuery(id+"F1.opRevolve","SWEPT_BODY",BODY,{"disambiguationData":[OSD([sQuery(id+"F0.wireOp",EDGE,"E0"),sQuery(id+"F0.wireOp",EDGE,"E3"),sQuery(id+"F0.wireOp",EDGE,"E4"),sQuery(id+"F0.wireOp",EDGE,"E5")])]}),"instanceName":"1"});
            var Q5;
            Q5=makeQuery(id+"F7.opPattern","COPY",BODY,{"derivedFrom":makeQuery(id+"F6.opPattern","COPY",BODY,{"derivedFrom":makeQuery(id+"F1.opRevolve","SWEPT_BODY",BODY,{"disambiguationData":[OSD([sQuery(id+"F0.wireOp",EDGE,"E0"),sQuery(id+"F0.wireOp",EDGE,"E3"),sQuery(id+"F0.wireOp",EDGE,"E4"),sQuery(id+"F0.wireOp",EDGE,"E5")])]}),"instanceName":"1"}),"instanceName":"1"});
            var Q6;
            Q6=makeQuery(id+"F6.opPattern","COPY",BODY,{"derivedFrom":makeQuery(id+"F5.opPattern","COPY",BODY,{"derivedFrom":makeQuery(id+"F1.opRevolve","SWEPT_BODY",BODY,{"disambiguationData":[OSD([sQuery(id+"F0.wireOp",EDGE,"E0"),sQuery(id+"F0.wireOp",EDGE,"E3"),sQuery(id+"F0.wireOp",EDGE,"E4"),sQuery(id+"F0.wireOp",EDGE,"E5")])]}),"instanceName":"1"}),"instanceName":"1"});
            var Q7;
            Q7=makeQuery(id+"F7.opPattern","COPY",BODY,{"derivedFrom":makeQuery(id+"F6.opPattern","COPY",BODY,{"derivedFrom":makeQuery(id+"F5.opPattern","COPY",BODY,{"derivedFrom":makeQuery(id+"F1.opRevolve","SWEPT_BODY",BODY,{"disambiguationData":[OSD([sQuery(id+"F0.wireOp",EDGE,"E0"),sQuery(id+"F0.wireOp",EDGE,"E3"),sQuery(id+"F0.wireOp",EDGE,"E4"),sQuery(id+"F0.wireOp",EDGE,"E5")])]}),"instanceName":"1"}),"instanceName":"1"}),"instanceName":"1"});
            var Q8;
            Q8=sQuery(id+"F3.wireOp",VERTEX,"E8.start");
            var Q9;
            Q9=sQuery(id+"F3.wireOp",VERTEX,"E72.end");
            transform(context, id + "F8", {"entities" : qUnion([Q0, Q1, Q2, Q3, Q4, Q5, Q6, Q7]), "transformType" : TransformType.TRANSLATION_ENTITY, "oppositeDirectionEntity" : false, "transformLine" : qUnion([Q8, Q9]), "makeCopy" : false});
        }
        {
            var Q0;
            Q0=makeQuery(id+"F7.opPattern","COPY",BODY,{"derivedFrom":makeQuery(id+"F5.opPattern","COPY",BODY,{"derivedFrom":makeQuery(id+"F1.opRevolve","SWEPT_BODY",BODY,{"disambiguationData":[OSD([sQuery(id+"F0.wireOp",EDGE,"E0"),sQuery(id+"F0.wireOp",EDGE,"E3"),sQuery(id+"F0.wireOp",EDGE,"E4"),sQuery(id+"F0.wireOp",EDGE,"E5")])]}),"instanceName":"1"}),"instanceName":"1"});
            var Q1;
            Q1=makeQuery(id+"F5.opPattern","COPY",BODY,{"derivedFrom":makeQuery(id+"F1.opRevolve","SWEPT_BODY",BODY,{"disambiguationData":[OSD([sQuery(id+"F0.wireOp",EDGE,"E0"),sQuery(id+"F0.wireOp",EDGE,"E3"),sQuery(id+"F0.wireOp",EDGE,"E4"),sQuery(id+"F0.wireOp",EDGE,"E5")])]}),"instanceName":"1"});
            var Q2;
            Q2=makeQuery(id+"F7.opPattern","COPY",BODY,{"derivedFrom":makeQuery(id+"F1.opRevolve","SWEPT_BODY",BODY,{"disambiguationData":[OSD([sQuery(id+"F0.wireOp",EDGE,"E0"),sQuery(id+"F0.wireOp",EDGE,"E3"),sQuery(id+"F0.wireOp",EDGE,"E4"),sQuery(id+"F0.wireOp",EDGE,"E5")])]}),"instanceName":"1"});
            var Q3;
            Q3=makeQuery(id+"F1.opRevolve","SWEPT_BODY",BODY,{"disambiguationData":[OSD([sQuery(id+"F0.wireOp",EDGE,"E0"),sQuery(id+"F0.wireOp",EDGE,"E3"),sQuery(id+"F0.wireOp",EDGE,"E4"),sQuery(id+"F0.wireOp",EDGE,"E5")])]});
            var Q4;
            Q4=makeQuery(id+"F7.opPattern","COPY",BODY,{"derivedFrom":makeQuery(id+"F6.opPattern","COPY",BODY,{"derivedFrom":makeQuery(id+"F5.opPattern","COPY",BODY,{"derivedFrom":makeQuery(id+"F1.opRevolve","SWEPT_BODY",BODY,{"disambiguationData":[OSD([sQuery(id+"F0.wireOp",EDGE,"E0"),sQuery(id+"F0.wireOp",EDGE,"E3"),sQuery(id+"F0.wireOp",EDGE,"E4"),sQuery(id+"F0.wireOp",EDGE,"E5")])]}),"instanceName":"1"}),"instanceName":"1"}),"instanceName":"1"});
            var Q5;
            Q5=makeQuery(id+"F6.opPattern","COPY",BODY,{"derivedFrom":makeQuery(id+"F5.opPattern","COPY",BODY,{"derivedFrom":makeQuery(id+"F1.opRevolve","SWEPT_BODY",BODY,{"disambiguationData":[OSD([sQuery(id+"F0.wireOp",EDGE,"E0"),sQuery(id+"F0.wireOp",EDGE,"E3"),sQuery(id+"F0.wireOp",EDGE,"E4"),sQuery(id+"F0.wireOp",EDGE,"E5")])]}),"instanceName":"1"}),"instanceName":"1"});
            var Q6;
            Q6=makeQuery(id+"F7.opPattern","COPY",BODY,{"derivedFrom":makeQuery(id+"F6.opPattern","COPY",BODY,{"derivedFrom":makeQuery(id+"F1.opRevolve","SWEPT_BODY",BODY,{"disambiguationData":[OSD([sQuery(id+"F0.wireOp",EDGE,"E0"),sQuery(id+"F0.wireOp",EDGE,"E3"),sQuery(id+"F0.wireOp",EDGE,"E4"),sQuery(id+"F0.wireOp",EDGE,"E5")])]}),"instanceName":"1"}),"instanceName":"1"});
            var Q7;
            Q7=makeQuery(id+"F6.opPattern","COPY",BODY,{"derivedFrom":makeQuery(id+"F1.opRevolve","SWEPT_BODY",BODY,{"disambiguationData":[OSD([sQuery(id+"F0.wireOp",EDGE,"E0"),sQuery(id+"F0.wireOp",EDGE,"E3"),sQuery(id+"F0.wireOp",EDGE,"E4"),sQuery(id+"F0.wireOp",EDGE,"E5")])]}),"instanceName":"1"});
            var Q8;
            Q8=sQuery(id+"F3.wireOp",VERTEX,"E9.right.start");
            var Q9;
            Q9=sQuery(id+"F3.wireOp",VERTEX,"E65.end");
            transform(context, id + "F9", {"entities" : qUnion([Q0, Q1, Q2, Q3, Q4, Q5, Q6, Q7]), "transformType" : TransformType.TRANSLATION_ENTITY, "oppositeDirectionEntity" : false, "transformLine" : qUnion([Q8, Q9]), "makeCopy" : true});
        }
        {
            var Q0;
            Q0=makeQuery(id+"F6.opPattern","COPY",BODY,{"derivedFrom":makeQuery(id+"F1.opRevolve","SWEPT_BODY",BODY,{"disambiguationData":[OSD([sQuery(id+"F0.wireOp",EDGE,"E0"),sQuery(id+"F0.wireOp",EDGE,"E3"),sQuery(id+"F0.wireOp",EDGE,"E4"),sQuery(id+"F0.wireOp",EDGE,"E5")])]}),"instanceName":"1"});
            var Q1;
            Q1=makeQuery(id+"F7.opPattern","COPY",BODY,{"derivedFrom":makeQuery(id+"F5.opPattern","COPY",BODY,{"derivedFrom":makeQuery(id+"F1.opRevolve","SWEPT_BODY",BODY,{"disambiguationData":[OSD([sQuery(id+"F0.wireOp",EDGE,"E0"),sQuery(id+"F0.wireOp",EDGE,"E3"),sQuery(id+"F0.wireOp",EDGE,"E4"),sQuery(id+"F0.wireOp",EDGE,"E5")])]}),"instanceName":"1"}),"instanceName":"1"});
            var Q2;
            Q2=makeQuery(id+"F5.opPattern","COPY",BODY,{"derivedFrom":makeQuery(id+"F1.opRevolve","SWEPT_BODY",BODY,{"disambiguationData":[OSD([sQuery(id+"F0.wireOp",EDGE,"E0"),sQuery(id+"F0.wireOp",EDGE,"E3"),sQuery(id+"F0.wireOp",EDGE,"E4"),sQuery(id+"F0.wireOp",EDGE,"E5")])]}),"instanceName":"1"});
            var Q3;
            Q3=makeQuery(id+"F7.opPattern","COPY",BODY,{"derivedFrom":makeQuery(id+"F1.opRevolve","SWEPT_BODY",BODY,{"disambiguationData":[OSD([sQuery(id+"F0.wireOp",EDGE,"E0"),sQuery(id+"F0.wireOp",EDGE,"E3"),sQuery(id+"F0.wireOp",EDGE,"E4"),sQuery(id+"F0.wireOp",EDGE,"E5")])]}),"instanceName":"1"});
            var Q4;
            Q4=makeQuery(id+"F1.opRevolve","SWEPT_BODY",BODY,{"disambiguationData":[OSD([sQuery(id+"F0.wireOp",EDGE,"E0"),sQuery(id+"F0.wireOp",EDGE,"E3"),sQuery(id+"F0.wireOp",EDGE,"E4"),sQuery(id+"F0.wireOp",EDGE,"E5")])]});
            var Q5;
            Q5=makeQuery(id+"F7.opPattern","COPY",BODY,{"derivedFrom":makeQuery(id+"F6.opPattern","COPY",BODY,{"derivedFrom":makeQuery(id+"F5.opPattern","COPY",BODY,{"derivedFrom":makeQuery(id+"F1.opRevolve","SWEPT_BODY",BODY,{"disambiguationData":[OSD([sQuery(id+"F0.wireOp",EDGE,"E0"),sQuery(id+"F0.wireOp",EDGE,"E3"),sQuery(id+"F0.wireOp",EDGE,"E4"),sQuery(id+"F0.wireOp",EDGE,"E5")])]}),"instanceName":"1"}),"instanceName":"1"}),"instanceName":"1"});
            var Q6;
            Q6=makeQuery(id+"F6.opPattern","COPY",BODY,{"derivedFrom":makeQuery(id+"F5.opPattern","COPY",BODY,{"derivedFrom":makeQuery(id+"F1.opRevolve","SWEPT_BODY",BODY,{"disambiguationData":[OSD([sQuery(id+"F0.wireOp",EDGE,"E0"),sQuery(id+"F0.wireOp",EDGE,"E3"),sQuery(id+"F0.wireOp",EDGE,"E4"),sQuery(id+"F0.wireOp",EDGE,"E5")])]}),"instanceName":"1"}),"instanceName":"1"});
            var Q7;
            Q7=makeQuery(id+"F7.opPattern","COPY",BODY,{"derivedFrom":makeQuery(id+"F6.opPattern","COPY",BODY,{"derivedFrom":makeQuery(id+"F1.opRevolve","SWEPT_BODY",BODY,{"disambiguationData":[OSD([sQuery(id+"F0.wireOp",EDGE,"E0"),sQuery(id+"F0.wireOp",EDGE,"E3"),sQuery(id+"F0.wireOp",EDGE,"E4"),sQuery(id+"F0.wireOp",EDGE,"E5")])]}),"instanceName":"1"}),"instanceName":"1"});
            var Q8;
            Q8=makeQuery(id+"F9.opPattern","COPY",BODY,{"derivedFrom":makeQuery(id+"F7.opPattern","COPY",BODY,{"derivedFrom":makeQuery(id+"F5.opPattern","COPY",BODY,{"derivedFrom":makeQuery(id+"F1.opRevolve","SWEPT_BODY",BODY,{"disambiguationData":[OSD([sQuery(id+"F0.wireOp",EDGE,"E0"),sQuery(id+"F0.wireOp",EDGE,"E3"),sQuery(id+"F0.wireOp",EDGE,"E4"),sQuery(id+"F0.wireOp",EDGE,"E5")])]}),"instanceName":"1"}),"instanceName":"1"}),"instanceName":"1"});
            var Q9;
            Q9=makeQuery(id+"F9.opPattern","COPY",BODY,{"derivedFrom":makeQuery(id+"F5.opPattern","COPY",BODY,{"derivedFrom":makeQuery(id+"F1.opRevolve","SWEPT_BODY",BODY,{"disambiguationData":[OSD([sQuery(id+"F0.wireOp",EDGE,"E0"),sQuery(id+"F0.wireOp",EDGE,"E3"),sQuery(id+"F0.wireOp",EDGE,"E4"),sQuery(id+"F0.wireOp",EDGE,"E5")])]}),"instanceName":"1"}),"instanceName":"1"});
            var Q10;
            Q10=makeQuery(id+"F9.opPattern","COPY",BODY,{"derivedFrom":makeQuery(id+"F7.opPattern","COPY",BODY,{"derivedFrom":makeQuery(id+"F1.opRevolve","SWEPT_BODY",BODY,{"disambiguationData":[OSD([sQuery(id+"F0.wireOp",EDGE,"E0"),sQuery(id+"F0.wireOp",EDGE,"E3"),sQuery(id+"F0.wireOp",EDGE,"E4"),sQuery(id+"F0.wireOp",EDGE,"E5")])]}),"instanceName":"1"}),"instanceName":"1"});
            var Q11;
            Q11=makeQuery(id+"F9.opPattern","COPY",BODY,{"derivedFrom":makeQuery(id+"F1.opRevolve","SWEPT_BODY",BODY,{"disambiguationData":[OSD([sQuery(id+"F0.wireOp",EDGE,"E0"),sQuery(id+"F0.wireOp",EDGE,"E3"),sQuery(id+"F0.wireOp",EDGE,"E4"),sQuery(id+"F0.wireOp",EDGE,"E5")])]}),"instanceName":"1"});
            var Q12;
            Q12=makeQuery(id+"F9.opPattern","COPY",BODY,{"derivedFrom":makeQuery(id+"F7.opPattern","COPY",BODY,{"derivedFrom":makeQuery(id+"F6.opPattern","COPY",BODY,{"derivedFrom":makeQuery(id+"F5.opPattern","COPY",BODY,{"derivedFrom":makeQuery(id+"F1.opRevolve","SWEPT_BODY",BODY,{"disambiguationData":[OSD([sQuery(id+"F0.wireOp",EDGE,"E0"),sQuery(id+"F0.wireOp",EDGE,"E3"),sQuery(id+"F0.wireOp",EDGE,"E4"),sQuery(id+"F0.wireOp",EDGE,"E5")])]}),"instanceName":"1"}),"instanceName":"1"}),"instanceName":"1"}),"instanceName":"1"});
            var Q13;
            Q13=makeQuery(id+"F9.opPattern","COPY",BODY,{"derivedFrom":makeQuery(id+"F6.opPattern","COPY",BODY,{"derivedFrom":makeQuery(id+"F5.opPattern","COPY",BODY,{"derivedFrom":makeQuery(id+"F1.opRevolve","SWEPT_BODY",BODY,{"disambiguationData":[OSD([sQuery(id+"F0.wireOp",EDGE,"E0"),sQuery(id+"F0.wireOp",EDGE,"E3"),sQuery(id+"F0.wireOp",EDGE,"E4"),sQuery(id+"F0.wireOp",EDGE,"E5")])]}),"instanceName":"1"}),"instanceName":"1"}),"instanceName":"1"});
            var Q14;
            Q14=makeQuery(id+"F9.opPattern","COPY",BODY,{"derivedFrom":makeQuery(id+"F7.opPattern","COPY",BODY,{"derivedFrom":makeQuery(id+"F6.opPattern","COPY",BODY,{"derivedFrom":makeQuery(id+"F1.opRevolve","SWEPT_BODY",BODY,{"disambiguationData":[OSD([sQuery(id+"F0.wireOp",EDGE,"E0"),sQuery(id+"F0.wireOp",EDGE,"E3"),sQuery(id+"F0.wireOp",EDGE,"E4"),sQuery(id+"F0.wireOp",EDGE,"E5")])]}),"instanceName":"1"}),"instanceName":"1"}),"instanceName":"1"});
            var Q15;
            Q15=makeQuery(id+"F9.opPattern","COPY",BODY,{"derivedFrom":makeQuery(id+"F6.opPattern","COPY",BODY,{"derivedFrom":makeQuery(id+"F1.opRevolve","SWEPT_BODY",BODY,{"disambiguationData":[OSD([sQuery(id+"F0.wireOp",EDGE,"E0"),sQuery(id+"F0.wireOp",EDGE,"E3"),sQuery(id+"F0.wireOp",EDGE,"E4"),sQuery(id+"F0.wireOp",EDGE,"E5")])]}),"instanceName":"1"}),"instanceName":"1"});
            var Q16;
            Q16=sQuery(id+"F3.wireOp",VERTEX,"E9.right.start");
            var Q17;
            Q17=sQuery(id+"F3.wireOp",VERTEX,"E7.end");
            transform(context, id + "F10", {"entities" : qUnion([Q0, Q1, Q2, Q3, Q4, Q5, Q6, Q7, Q8, Q9, Q10, Q11, Q12, Q13, Q14, Q15]), "transformType" : TransformType.TRANSLATION_ENTITY, "oppositeDirectionEntity" : false, "transformLine" : qUnion([Q16, Q17]), "makeCopy" : true});
        }
        {
            var Q0;
            Q0=makeQuery(id+"F10.opPattern","COPY",BODY,{"derivedFrom":makeQuery(id+"F6.opPattern","COPY",BODY,{"derivedFrom":makeQuery(id+"F1.opRevolve","SWEPT_BODY",BODY,{"disambiguationData":[OSD([sQuery(id+"F0.wireOp",EDGE,"E0"),sQuery(id+"F0.wireOp",EDGE,"E3"),sQuery(id+"F0.wireOp",EDGE,"E4"),sQuery(id+"F0.wireOp",EDGE,"E5")])]}),"instanceName":"1"}),"instanceName":"1"});
            var Q1;
            Q1=makeQuery(id+"F10.opPattern","COPY",BODY,{"derivedFrom":makeQuery(id+"F7.opPattern","COPY",BODY,{"derivedFrom":makeQuery(id+"F5.opPattern","COPY",BODY,{"derivedFrom":makeQuery(id+"F1.opRevolve","SWEPT_BODY",BODY,{"disambiguationData":[OSD([sQuery(id+"F0.wireOp",EDGE,"E0"),sQuery(id+"F0.wireOp",EDGE,"E3"),sQuery(id+"F0.wireOp",EDGE,"E4"),sQuery(id+"F0.wireOp",EDGE,"E5")])]}),"instanceName":"1"}),"instanceName":"1"}),"instanceName":"1"});
            var Q2;
            Q2=makeQuery(id+"F10.opPattern","COPY",BODY,{"derivedFrom":makeQuery(id+"F5.opPattern","COPY",BODY,{"derivedFrom":makeQuery(id+"F1.opRevolve","SWEPT_BODY",BODY,{"disambiguationData":[OSD([sQuery(id+"F0.wireOp",EDGE,"E0"),sQuery(id+"F0.wireOp",EDGE,"E3"),sQuery(id+"F0.wireOp",EDGE,"E4"),sQuery(id+"F0.wireOp",EDGE,"E5")])]}),"instanceName":"1"}),"instanceName":"1"});
            var Q3;
            Q3=makeQuery(id+"F10.opPattern","COPY",BODY,{"derivedFrom":makeQuery(id+"F7.opPattern","COPY",BODY,{"derivedFrom":makeQuery(id+"F1.opRevolve","SWEPT_BODY",BODY,{"disambiguationData":[OSD([sQuery(id+"F0.wireOp",EDGE,"E0"),sQuery(id+"F0.wireOp",EDGE,"E3"),sQuery(id+"F0.wireOp",EDGE,"E4"),sQuery(id+"F0.wireOp",EDGE,"E5")])]}),"instanceName":"1"}),"instanceName":"1"});
            var Q4;
            Q4=makeQuery(id+"F10.opPattern","COPY",BODY,{"derivedFrom":makeQuery(id+"F1.opRevolve","SWEPT_BODY",BODY,{"disambiguationData":[OSD([sQuery(id+"F0.wireOp",EDGE,"E0"),sQuery(id+"F0.wireOp",EDGE,"E3"),sQuery(id+"F0.wireOp",EDGE,"E4"),sQuery(id+"F0.wireOp",EDGE,"E5")])]}),"instanceName":"1"});
            var Q5;
            Q5=makeQuery(id+"F10.opPattern","COPY",BODY,{"derivedFrom":makeQuery(id+"F7.opPattern","COPY",BODY,{"derivedFrom":makeQuery(id+"F6.opPattern","COPY",BODY,{"derivedFrom":makeQuery(id+"F5.opPattern","COPY",BODY,{"derivedFrom":makeQuery(id+"F1.opRevolve","SWEPT_BODY",BODY,{"disambiguationData":[OSD([sQuery(id+"F0.wireOp",EDGE,"E0"),sQuery(id+"F0.wireOp",EDGE,"E3"),sQuery(id+"F0.wireOp",EDGE,"E4"),sQuery(id+"F0.wireOp",EDGE,"E5")])]}),"instanceName":"1"}),"instanceName":"1"}),"instanceName":"1"}),"instanceName":"1"});
            var Q6;
            Q6=makeQuery(id+"F10.opPattern","COPY",BODY,{"derivedFrom":makeQuery(id+"F6.opPattern","COPY",BODY,{"derivedFrom":makeQuery(id+"F5.opPattern","COPY",BODY,{"derivedFrom":makeQuery(id+"F1.opRevolve","SWEPT_BODY",BODY,{"disambiguationData":[OSD([sQuery(id+"F0.wireOp",EDGE,"E0"),sQuery(id+"F0.wireOp",EDGE,"E3"),sQuery(id+"F0.wireOp",EDGE,"E4"),sQuery(id+"F0.wireOp",EDGE,"E5")])]}),"instanceName":"1"}),"instanceName":"1"}),"instanceName":"1"});
            var Q7;
            Q7=makeQuery(id+"F10.opPattern","COPY",BODY,{"derivedFrom":makeQuery(id+"F7.opPattern","COPY",BODY,{"derivedFrom":makeQuery(id+"F6.opPattern","COPY",BODY,{"derivedFrom":makeQuery(id+"F1.opRevolve","SWEPT_BODY",BODY,{"disambiguationData":[OSD([sQuery(id+"F0.wireOp",EDGE,"E0"),sQuery(id+"F0.wireOp",EDGE,"E3"),sQuery(id+"F0.wireOp",EDGE,"E4"),sQuery(id+"F0.wireOp",EDGE,"E5")])]}),"instanceName":"1"}),"instanceName":"1"}),"instanceName":"1"});
            var Q8;
            Q8=makeQuery(id+"F7.opPattern","COPY",BODY,{"derivedFrom":makeQuery(id+"F6.opPattern","COPY",BODY,{"derivedFrom":makeQuery(id+"F1.opRevolve","SWEPT_BODY",BODY,{"disambiguationData":[OSD([sQuery(id+"F0.wireOp",EDGE,"E0"),sQuery(id+"F0.wireOp",EDGE,"E3"),sQuery(id+"F0.wireOp",EDGE,"E4"),sQuery(id+"F0.wireOp",EDGE,"E5")])]}),"instanceName":"1"}),"instanceName":"1"});
            var Q9;
            Q9=makeQuery(id+"F6.opPattern","COPY",BODY,{"derivedFrom":makeQuery(id+"F1.opRevolve","SWEPT_BODY",BODY,{"disambiguationData":[OSD([sQuery(id+"F0.wireOp",EDGE,"E0"),sQuery(id+"F0.wireOp",EDGE,"E3"),sQuery(id+"F0.wireOp",EDGE,"E4"),sQuery(id+"F0.wireOp",EDGE,"E5")])]}),"instanceName":"1"});
            var Q10;
            Q10=makeQuery(id+"F7.opPattern","COPY",BODY,{"derivedFrom":makeQuery(id+"F5.opPattern","COPY",BODY,{"derivedFrom":makeQuery(id+"F1.opRevolve","SWEPT_BODY",BODY,{"disambiguationData":[OSD([sQuery(id+"F0.wireOp",EDGE,"E0"),sQuery(id+"F0.wireOp",EDGE,"E3"),sQuery(id+"F0.wireOp",EDGE,"E4"),sQuery(id+"F0.wireOp",EDGE,"E5")])]}),"instanceName":"1"}),"instanceName":"1"});
            var Q11;
            Q11=makeQuery(id+"F5.opPattern","COPY",BODY,{"derivedFrom":makeQuery(id+"F1.opRevolve","SWEPT_BODY",BODY,{"disambiguationData":[OSD([sQuery(id+"F0.wireOp",EDGE,"E0"),sQuery(id+"F0.wireOp",EDGE,"E3"),sQuery(id+"F0.wireOp",EDGE,"E4"),sQuery(id+"F0.wireOp",EDGE,"E5")])]}),"instanceName":"1"});
            var Q12;
            Q12=makeQuery(id+"F7.opPattern","COPY",BODY,{"derivedFrom":makeQuery(id+"F1.opRevolve","SWEPT_BODY",BODY,{"disambiguationData":[OSD([sQuery(id+"F0.wireOp",EDGE,"E0"),sQuery(id+"F0.wireOp",EDGE,"E3"),sQuery(id+"F0.wireOp",EDGE,"E4"),sQuery(id+"F0.wireOp",EDGE,"E5")])]}),"instanceName":"1"});
            var Q13;
            Q13=makeQuery(id+"F1.opRevolve","SWEPT_BODY",BODY,{"disambiguationData":[OSD([sQuery(id+"F0.wireOp",EDGE,"E0"),sQuery(id+"F0.wireOp",EDGE,"E3"),sQuery(id+"F0.wireOp",EDGE,"E4"),sQuery(id+"F0.wireOp",EDGE,"E5")])]});
            var Q14;
            Q14=makeQuery(id+"F7.opPattern","COPY",BODY,{"derivedFrom":makeQuery(id+"F6.opPattern","COPY",BODY,{"derivedFrom":makeQuery(id+"F5.opPattern","COPY",BODY,{"derivedFrom":makeQuery(id+"F1.opRevolve","SWEPT_BODY",BODY,{"disambiguationData":[OSD([sQuery(id+"F0.wireOp",EDGE,"E0"),sQuery(id+"F0.wireOp",EDGE,"E3"),sQuery(id+"F0.wireOp",EDGE,"E4"),sQuery(id+"F0.wireOp",EDGE,"E5")])]}),"instanceName":"1"}),"instanceName":"1"}),"instanceName":"1"});
            var Q15;
            Q15=makeQuery(id+"F6.opPattern","COPY",BODY,{"derivedFrom":makeQuery(id+"F5.opPattern","COPY",BODY,{"derivedFrom":makeQuery(id+"F1.opRevolve","SWEPT_BODY",BODY,{"disambiguationData":[OSD([sQuery(id+"F0.wireOp",EDGE,"E0"),sQuery(id+"F0.wireOp",EDGE,"E3"),sQuery(id+"F0.wireOp",EDGE,"E4"),sQuery(id+"F0.wireOp",EDGE,"E5")])]}),"instanceName":"1"}),"instanceName":"1"});
            var Q16;
            Q16=makeQuery(id+"F10.opPattern","COPY",BODY,{"derivedFrom":makeQuery(id+"F9.opPattern","COPY",BODY,{"derivedFrom":makeQuery(id+"F6.opPattern","COPY",BODY,{"derivedFrom":makeQuery(id+"F5.opPattern","COPY",BODY,{"derivedFrom":makeQuery(id+"F1.opRevolve","SWEPT_BODY",BODY,{"disambiguationData":[OSD([sQuery(id+"F0.wireOp",EDGE,"E0"),sQuery(id+"F0.wireOp",EDGE,"E3"),sQuery(id+"F0.wireOp",EDGE,"E4"),sQuery(id+"F0.wireOp",EDGE,"E5")])]}),"instanceName":"1"}),"instanceName":"1"}),"instanceName":"1"}),"instanceName":"1"});
            var Q17;
            Q17=makeQuery(id+"F10.opPattern","COPY",BODY,{"derivedFrom":makeQuery(id+"F9.opPattern","COPY",BODY,{"derivedFrom":makeQuery(id+"F7.opPattern","COPY",BODY,{"derivedFrom":makeQuery(id+"F6.opPattern","COPY",BODY,{"derivedFrom":makeQuery(id+"F1.opRevolve","SWEPT_BODY",BODY,{"disambiguationData":[OSD([sQuery(id+"F0.wireOp",EDGE,"E0"),sQuery(id+"F0.wireOp",EDGE,"E3"),sQuery(id+"F0.wireOp",EDGE,"E4"),sQuery(id+"F0.wireOp",EDGE,"E5")])]}),"instanceName":"1"}),"instanceName":"1"}),"instanceName":"1"}),"instanceName":"1"});
            var Q18;
            Q18=makeQuery(id+"F10.opPattern","COPY",BODY,{"derivedFrom":makeQuery(id+"F9.opPattern","COPY",BODY,{"derivedFrom":makeQuery(id+"F6.opPattern","COPY",BODY,{"derivedFrom":makeQuery(id+"F1.opRevolve","SWEPT_BODY",BODY,{"disambiguationData":[OSD([sQuery(id+"F0.wireOp",EDGE,"E0"),sQuery(id+"F0.wireOp",EDGE,"E3"),sQuery(id+"F0.wireOp",EDGE,"E4"),sQuery(id+"F0.wireOp",EDGE,"E5")])]}),"instanceName":"1"}),"instanceName":"1"}),"instanceName":"1"});
            var Q19;
            Q19=makeQuery(id+"F10.opPattern","COPY",BODY,{"derivedFrom":makeQuery(id+"F9.opPattern","COPY",BODY,{"derivedFrom":makeQuery(id+"F7.opPattern","COPY",BODY,{"derivedFrom":makeQuery(id+"F5.opPattern","COPY",BODY,{"derivedFrom":makeQuery(id+"F1.opRevolve","SWEPT_BODY",BODY,{"disambiguationData":[OSD([sQuery(id+"F0.wireOp",EDGE,"E0"),sQuery(id+"F0.wireOp",EDGE,"E3"),sQuery(id+"F0.wireOp",EDGE,"E4"),sQuery(id+"F0.wireOp",EDGE,"E5")])]}),"instanceName":"1"}),"instanceName":"1"}),"instanceName":"1"}),"instanceName":"1"});
            var Q20;
            Q20=makeQuery(id+"F10.opPattern","COPY",BODY,{"derivedFrom":makeQuery(id+"F9.opPattern","COPY",BODY,{"derivedFrom":makeQuery(id+"F5.opPattern","COPY",BODY,{"derivedFrom":makeQuery(id+"F1.opRevolve","SWEPT_BODY",BODY,{"disambiguationData":[OSD([sQuery(id+"F0.wireOp",EDGE,"E0"),sQuery(id+"F0.wireOp",EDGE,"E3"),sQuery(id+"F0.wireOp",EDGE,"E4"),sQuery(id+"F0.wireOp",EDGE,"E5")])]}),"instanceName":"1"}),"instanceName":"1"}),"instanceName":"1"});
            var Q21;
            Q21=makeQuery(id+"F10.opPattern","COPY",BODY,{"derivedFrom":makeQuery(id+"F9.opPattern","COPY",BODY,{"derivedFrom":makeQuery(id+"F7.opPattern","COPY",BODY,{"derivedFrom":makeQuery(id+"F1.opRevolve","SWEPT_BODY",BODY,{"disambiguationData":[OSD([sQuery(id+"F0.wireOp",EDGE,"E0"),sQuery(id+"F0.wireOp",EDGE,"E3"),sQuery(id+"F0.wireOp",EDGE,"E4"),sQuery(id+"F0.wireOp",EDGE,"E5")])]}),"instanceName":"1"}),"instanceName":"1"}),"instanceName":"1"});
            var Q22;
            Q22=makeQuery(id+"F10.opPattern","COPY",BODY,{"derivedFrom":makeQuery(id+"F9.opPattern","COPY",BODY,{"derivedFrom":makeQuery(id+"F1.opRevolve","SWEPT_BODY",BODY,{"disambiguationData":[OSD([sQuery(id+"F0.wireOp",EDGE,"E0"),sQuery(id+"F0.wireOp",EDGE,"E3"),sQuery(id+"F0.wireOp",EDGE,"E4"),sQuery(id+"F0.wireOp",EDGE,"E5")])]}),"instanceName":"1"}),"instanceName":"1"});
            var Q23;
            Q23=makeQuery(id+"F10.opPattern","COPY",BODY,{"derivedFrom":makeQuery(id+"F9.opPattern","COPY",BODY,{"derivedFrom":makeQuery(id+"F7.opPattern","COPY",BODY,{"derivedFrom":makeQuery(id+"F6.opPattern","COPY",BODY,{"derivedFrom":makeQuery(id+"F5.opPattern","COPY",BODY,{"derivedFrom":makeQuery(id+"F1.opRevolve","SWEPT_BODY",BODY,{"disambiguationData":[OSD([sQuery(id+"F0.wireOp",EDGE,"E0"),sQuery(id+"F0.wireOp",EDGE,"E3"),sQuery(id+"F0.wireOp",EDGE,"E4"),sQuery(id+"F0.wireOp",EDGE,"E5")])]}),"instanceName":"1"}),"instanceName":"1"}),"instanceName":"1"}),"instanceName":"1"}),"instanceName":"1"});
            var Q24;
            Q24=makeQuery(id+"F9.opPattern","COPY",BODY,{"derivedFrom":makeQuery(id+"F7.opPattern","COPY",BODY,{"derivedFrom":makeQuery(id+"F6.opPattern","COPY",BODY,{"derivedFrom":makeQuery(id+"F5.opPattern","COPY",BODY,{"derivedFrom":makeQuery(id+"F1.opRevolve","SWEPT_BODY",BODY,{"disambiguationData":[OSD([sQuery(id+"F0.wireOp",EDGE,"E0"),sQuery(id+"F0.wireOp",EDGE,"E3"),sQuery(id+"F0.wireOp",EDGE,"E4"),sQuery(id+"F0.wireOp",EDGE,"E5")])]}),"instanceName":"1"}),"instanceName":"1"}),"instanceName":"1"}),"instanceName":"1"});
            var Q25;
            Q25=makeQuery(id+"F9.opPattern","COPY",BODY,{"derivedFrom":makeQuery(id+"F6.opPattern","COPY",BODY,{"derivedFrom":makeQuery(id+"F5.opPattern","COPY",BODY,{"derivedFrom":makeQuery(id+"F1.opRevolve","SWEPT_BODY",BODY,{"disambiguationData":[OSD([sQuery(id+"F0.wireOp",EDGE,"E0"),sQuery(id+"F0.wireOp",EDGE,"E3"),sQuery(id+"F0.wireOp",EDGE,"E4"),sQuery(id+"F0.wireOp",EDGE,"E5")])]}),"instanceName":"1"}),"instanceName":"1"}),"instanceName":"1"});
            var Q26;
            Q26=makeQuery(id+"F9.opPattern","COPY",BODY,{"derivedFrom":makeQuery(id+"F7.opPattern","COPY",BODY,{"derivedFrom":makeQuery(id+"F6.opPattern","COPY",BODY,{"derivedFrom":makeQuery(id+"F1.opRevolve","SWEPT_BODY",BODY,{"disambiguationData":[OSD([sQuery(id+"F0.wireOp",EDGE,"E0"),sQuery(id+"F0.wireOp",EDGE,"E3"),sQuery(id+"F0.wireOp",EDGE,"E4"),sQuery(id+"F0.wireOp",EDGE,"E5")])]}),"instanceName":"1"}),"instanceName":"1"}),"instanceName":"1"});
            var Q27;
            Q27=makeQuery(id+"F9.opPattern","COPY",BODY,{"derivedFrom":makeQuery(id+"F6.opPattern","COPY",BODY,{"derivedFrom":makeQuery(id+"F1.opRevolve","SWEPT_BODY",BODY,{"disambiguationData":[OSD([sQuery(id+"F0.wireOp",EDGE,"E0"),sQuery(id+"F0.wireOp",EDGE,"E3"),sQuery(id+"F0.wireOp",EDGE,"E4"),sQuery(id+"F0.wireOp",EDGE,"E5")])]}),"instanceName":"1"}),"instanceName":"1"});
            var Q28;
            Q28=makeQuery(id+"F9.opPattern","COPY",BODY,{"derivedFrom":makeQuery(id+"F7.opPattern","COPY",BODY,{"derivedFrom":makeQuery(id+"F5.opPattern","COPY",BODY,{"derivedFrom":makeQuery(id+"F1.opRevolve","SWEPT_BODY",BODY,{"disambiguationData":[OSD([sQuery(id+"F0.wireOp",EDGE,"E0"),sQuery(id+"F0.wireOp",EDGE,"E3"),sQuery(id+"F0.wireOp",EDGE,"E4"),sQuery(id+"F0.wireOp",EDGE,"E5")])]}),"instanceName":"1"}),"instanceName":"1"}),"instanceName":"1"});
            var Q29;
            Q29=makeQuery(id+"F9.opPattern","COPY",BODY,{"derivedFrom":makeQuery(id+"F5.opPattern","COPY",BODY,{"derivedFrom":makeQuery(id+"F1.opRevolve","SWEPT_BODY",BODY,{"disambiguationData":[OSD([sQuery(id+"F0.wireOp",EDGE,"E0"),sQuery(id+"F0.wireOp",EDGE,"E3"),sQuery(id+"F0.wireOp",EDGE,"E4"),sQuery(id+"F0.wireOp",EDGE,"E5")])]}),"instanceName":"1"}),"instanceName":"1"});
            var Q30;
            Q30=makeQuery(id+"F9.opPattern","COPY",BODY,{"derivedFrom":makeQuery(id+"F7.opPattern","COPY",BODY,{"derivedFrom":makeQuery(id+"F1.opRevolve","SWEPT_BODY",BODY,{"disambiguationData":[OSD([sQuery(id+"F0.wireOp",EDGE,"E0"),sQuery(id+"F0.wireOp",EDGE,"E3"),sQuery(id+"F0.wireOp",EDGE,"E4"),sQuery(id+"F0.wireOp",EDGE,"E5")])]}),"instanceName":"1"}),"instanceName":"1"});
            var Q31;
            Q31=makeQuery(id+"F9.opPattern","COPY",BODY,{"derivedFrom":makeQuery(id+"F1.opRevolve","SWEPT_BODY",BODY,{"disambiguationData":[OSD([sQuery(id+"F0.wireOp",EDGE,"E0"),sQuery(id+"F0.wireOp",EDGE,"E3"),sQuery(id+"F0.wireOp",EDGE,"E4"),sQuery(id+"F0.wireOp",EDGE,"E5")])]}),"instanceName":"1"});
            var Q32;
            Q32=sQuery(id+"F3.wireOp",VERTEX,"E9.right.start");
            var Q33;
            Q33=sQuery(id+"F3.wireOp",VERTEX,"E19.end");
            transform(context, id + "F11", {"entities" : qUnion([Q0, Q1, Q2, Q3, Q4, Q5, Q6, Q7, Q8, Q9, Q10, Q11, Q12, Q13, Q14, Q15, Q16, Q17, Q18, Q19, Q20, Q21, Q22, Q23, Q24, Q25, Q26, Q27, Q28, Q29, Q30, Q31]), "transformType" : TransformType.TRANSLATION_ENTITY, "oppositeDirectionEntity" : false, "transformLine" : qUnion([Q32, Q33]), "makeCopy" : false});
        }
        {
            var Q0;
            Q0=makeQuery(id+"F9.opPattern","COPY",BODY,{"derivedFrom":makeQuery(id+"F5.opPattern","COPY",BODY,{"derivedFrom":makeQuery(id+"F1.opRevolve","SWEPT_BODY",BODY,{"disambiguationData":[OSD([sQuery(id+"F0.wireOp",EDGE,"E0"),sQuery(id+"F0.wireOp",EDGE,"E3"),sQuery(id+"F0.wireOp",EDGE,"E4"),sQuery(id+"F0.wireOp",EDGE,"E5")])]}),"instanceName":"1"}),"instanceName":"1"});
            var Q1;
            Q1=makeQuery(id+"F9.opPattern","COPY",BODY,{"derivedFrom":makeQuery(id+"F7.opPattern","COPY",BODY,{"derivedFrom":makeQuery(id+"F1.opRevolve","SWEPT_BODY",BODY,{"disambiguationData":[OSD([sQuery(id+"F0.wireOp",EDGE,"E0"),sQuery(id+"F0.wireOp",EDGE,"E3"),sQuery(id+"F0.wireOp",EDGE,"E4"),sQuery(id+"F0.wireOp",EDGE,"E5")])]}),"instanceName":"1"}),"instanceName":"1"});
            var Q2;
            Q2=makeQuery(id+"F9.opPattern","COPY",BODY,{"derivedFrom":makeQuery(id+"F1.opRevolve","SWEPT_BODY",BODY,{"disambiguationData":[OSD([sQuery(id+"F0.wireOp",EDGE,"E0"),sQuery(id+"F0.wireOp",EDGE,"E3"),sQuery(id+"F0.wireOp",EDGE,"E4"),sQuery(id+"F0.wireOp",EDGE,"E5")])]}),"instanceName":"1"});
            var Q3;
            Q3=makeQuery(id+"F9.opPattern","COPY",BODY,{"derivedFrom":makeQuery(id+"F7.opPattern","COPY",BODY,{"derivedFrom":makeQuery(id+"F6.opPattern","COPY",BODY,{"derivedFrom":makeQuery(id+"F5.opPattern","COPY",BODY,{"derivedFrom":makeQuery(id+"F1.opRevolve","SWEPT_BODY",BODY,{"disambiguationData":[OSD([sQuery(id+"F0.wireOp",EDGE,"E0"),sQuery(id+"F0.wireOp",EDGE,"E3"),sQuery(id+"F0.wireOp",EDGE,"E4"),sQuery(id+"F0.wireOp",EDGE,"E5")])]}),"instanceName":"1"}),"instanceName":"1"}),"instanceName":"1"}),"instanceName":"1"});
            var Q4;
            Q4=makeQuery(id+"F9.opPattern","COPY",BODY,{"derivedFrom":makeQuery(id+"F6.opPattern","COPY",BODY,{"derivedFrom":makeQuery(id+"F5.opPattern","COPY",BODY,{"derivedFrom":makeQuery(id+"F1.opRevolve","SWEPT_BODY",BODY,{"disambiguationData":[OSD([sQuery(id+"F0.wireOp",EDGE,"E0"),sQuery(id+"F0.wireOp",EDGE,"E3"),sQuery(id+"F0.wireOp",EDGE,"E4"),sQuery(id+"F0.wireOp",EDGE,"E5")])]}),"instanceName":"1"}),"instanceName":"1"}),"instanceName":"1"});
            var Q5;
            Q5=makeQuery(id+"F9.opPattern","COPY",BODY,{"derivedFrom":makeQuery(id+"F7.opPattern","COPY",BODY,{"derivedFrom":makeQuery(id+"F6.opPattern","COPY",BODY,{"derivedFrom":makeQuery(id+"F1.opRevolve","SWEPT_BODY",BODY,{"disambiguationData":[OSD([sQuery(id+"F0.wireOp",EDGE,"E0"),sQuery(id+"F0.wireOp",EDGE,"E3"),sQuery(id+"F0.wireOp",EDGE,"E4"),sQuery(id+"F0.wireOp",EDGE,"E5")])]}),"instanceName":"1"}),"instanceName":"1"}),"instanceName":"1"});
            var Q6;
            Q6=makeQuery(id+"F9.opPattern","COPY",BODY,{"derivedFrom":makeQuery(id+"F6.opPattern","COPY",BODY,{"derivedFrom":makeQuery(id+"F1.opRevolve","SWEPT_BODY",BODY,{"disambiguationData":[OSD([sQuery(id+"F0.wireOp",EDGE,"E0"),sQuery(id+"F0.wireOp",EDGE,"E3"),sQuery(id+"F0.wireOp",EDGE,"E4"),sQuery(id+"F0.wireOp",EDGE,"E5")])]}),"instanceName":"1"}),"instanceName":"1"});
            var Q7;
            Q7=makeQuery(id+"F9.opPattern","COPY",BODY,{"derivedFrom":makeQuery(id+"F7.opPattern","COPY",BODY,{"derivedFrom":makeQuery(id+"F5.opPattern","COPY",BODY,{"derivedFrom":makeQuery(id+"F1.opRevolve","SWEPT_BODY",BODY,{"disambiguationData":[OSD([sQuery(id+"F0.wireOp",EDGE,"E0"),sQuery(id+"F0.wireOp",EDGE,"E3"),sQuery(id+"F0.wireOp",EDGE,"E4"),sQuery(id+"F0.wireOp",EDGE,"E5")])]}),"instanceName":"1"}),"instanceName":"1"}),"instanceName":"1"});
            var Q8;
            Q8=makeQuery(id+"F10.opPattern","COPY",BODY,{"derivedFrom":makeQuery(id+"F9.opPattern","COPY",BODY,{"derivedFrom":makeQuery(id+"F7.opPattern","COPY",BODY,{"derivedFrom":makeQuery(id+"F5.opPattern","COPY",BODY,{"derivedFrom":makeQuery(id+"F1.opRevolve","SWEPT_BODY",BODY,{"disambiguationData":[OSD([sQuery(id+"F0.wireOp",EDGE,"E0"),sQuery(id+"F0.wireOp",EDGE,"E3"),sQuery(id+"F0.wireOp",EDGE,"E4"),sQuery(id+"F0.wireOp",EDGE,"E5")])]}),"instanceName":"1"}),"instanceName":"1"}),"instanceName":"1"}),"instanceName":"1"});
            var Q9;
            Q9=makeQuery(id+"F10.opPattern","COPY",BODY,{"derivedFrom":makeQuery(id+"F9.opPattern","COPY",BODY,{"derivedFrom":makeQuery(id+"F5.opPattern","COPY",BODY,{"derivedFrom":makeQuery(id+"F1.opRevolve","SWEPT_BODY",BODY,{"disambiguationData":[OSD([sQuery(id+"F0.wireOp",EDGE,"E0"),sQuery(id+"F0.wireOp",EDGE,"E3"),sQuery(id+"F0.wireOp",EDGE,"E4"),sQuery(id+"F0.wireOp",EDGE,"E5")])]}),"instanceName":"1"}),"instanceName":"1"}),"instanceName":"1"});
            var Q10;
            Q10=makeQuery(id+"F10.opPattern","COPY",BODY,{"derivedFrom":makeQuery(id+"F9.opPattern","COPY",BODY,{"derivedFrom":makeQuery(id+"F7.opPattern","COPY",BODY,{"derivedFrom":makeQuery(id+"F1.opRevolve","SWEPT_BODY",BODY,{"disambiguationData":[OSD([sQuery(id+"F0.wireOp",EDGE,"E0"),sQuery(id+"F0.wireOp",EDGE,"E3"),sQuery(id+"F0.wireOp",EDGE,"E4"),sQuery(id+"F0.wireOp",EDGE,"E5")])]}),"instanceName":"1"}),"instanceName":"1"}),"instanceName":"1"});
            var Q11;
            Q11=makeQuery(id+"F10.opPattern","COPY",BODY,{"derivedFrom":makeQuery(id+"F9.opPattern","COPY",BODY,{"derivedFrom":makeQuery(id+"F1.opRevolve","SWEPT_BODY",BODY,{"disambiguationData":[OSD([sQuery(id+"F0.wireOp",EDGE,"E0"),sQuery(id+"F0.wireOp",EDGE,"E3"),sQuery(id+"F0.wireOp",EDGE,"E4"),sQuery(id+"F0.wireOp",EDGE,"E5")])]}),"instanceName":"1"}),"instanceName":"1"});
            var Q12;
            Q12=makeQuery(id+"F10.opPattern","COPY",BODY,{"derivedFrom":makeQuery(id+"F9.opPattern","COPY",BODY,{"derivedFrom":makeQuery(id+"F7.opPattern","COPY",BODY,{"derivedFrom":makeQuery(id+"F6.opPattern","COPY",BODY,{"derivedFrom":makeQuery(id+"F5.opPattern","COPY",BODY,{"derivedFrom":makeQuery(id+"F1.opRevolve","SWEPT_BODY",BODY,{"disambiguationData":[OSD([sQuery(id+"F0.wireOp",EDGE,"E0"),sQuery(id+"F0.wireOp",EDGE,"E3"),sQuery(id+"F0.wireOp",EDGE,"E4"),sQuery(id+"F0.wireOp",EDGE,"E5")])]}),"instanceName":"1"}),"instanceName":"1"}),"instanceName":"1"}),"instanceName":"1"}),"instanceName":"1"});
            var Q13;
            Q13=makeQuery(id+"F10.opPattern","COPY",BODY,{"derivedFrom":makeQuery(id+"F9.opPattern","COPY",BODY,{"derivedFrom":makeQuery(id+"F6.opPattern","COPY",BODY,{"derivedFrom":makeQuery(id+"F5.opPattern","COPY",BODY,{"derivedFrom":makeQuery(id+"F1.opRevolve","SWEPT_BODY",BODY,{"disambiguationData":[OSD([sQuery(id+"F0.wireOp",EDGE,"E0"),sQuery(id+"F0.wireOp",EDGE,"E3"),sQuery(id+"F0.wireOp",EDGE,"E4"),sQuery(id+"F0.wireOp",EDGE,"E5")])]}),"instanceName":"1"}),"instanceName":"1"}),"instanceName":"1"}),"instanceName":"1"});
            var Q14;
            Q14=makeQuery(id+"F10.opPattern","COPY",BODY,{"derivedFrom":makeQuery(id+"F9.opPattern","COPY",BODY,{"derivedFrom":makeQuery(id+"F7.opPattern","COPY",BODY,{"derivedFrom":makeQuery(id+"F6.opPattern","COPY",BODY,{"derivedFrom":makeQuery(id+"F1.opRevolve","SWEPT_BODY",BODY,{"disambiguationData":[OSD([sQuery(id+"F0.wireOp",EDGE,"E0"),sQuery(id+"F0.wireOp",EDGE,"E3"),sQuery(id+"F0.wireOp",EDGE,"E4"),sQuery(id+"F0.wireOp",EDGE,"E5")])]}),"instanceName":"1"}),"instanceName":"1"}),"instanceName":"1"}),"instanceName":"1"});
            var Q15;
            Q15=makeQuery(id+"F10.opPattern","COPY",BODY,{"derivedFrom":makeQuery(id+"F9.opPattern","COPY",BODY,{"derivedFrom":makeQuery(id+"F6.opPattern","COPY",BODY,{"derivedFrom":makeQuery(id+"F1.opRevolve","SWEPT_BODY",BODY,{"disambiguationData":[OSD([sQuery(id+"F0.wireOp",EDGE,"E0"),sQuery(id+"F0.wireOp",EDGE,"E3"),sQuery(id+"F0.wireOp",EDGE,"E4"),sQuery(id+"F0.wireOp",EDGE,"E5")])]}),"instanceName":"1"}),"instanceName":"1"}),"instanceName":"1"});
            var Q16;
            Q16=makeQuery(id+"F6.opPattern","COPY",BODY,{"derivedFrom":makeQuery(id+"F1.opRevolve","SWEPT_BODY",BODY,{"disambiguationData":[OSD([sQuery(id+"F0.wireOp",EDGE,"E0"),sQuery(id+"F0.wireOp",EDGE,"E3"),sQuery(id+"F0.wireOp",EDGE,"E4"),sQuery(id+"F0.wireOp",EDGE,"E5")])]}),"instanceName":"1"});
            var Q17;
            Q17=makeQuery(id+"F7.opPattern","COPY",BODY,{"derivedFrom":makeQuery(id+"F5.opPattern","COPY",BODY,{"derivedFrom":makeQuery(id+"F1.opRevolve","SWEPT_BODY",BODY,{"disambiguationData":[OSD([sQuery(id+"F0.wireOp",EDGE,"E0"),sQuery(id+"F0.wireOp",EDGE,"E3"),sQuery(id+"F0.wireOp",EDGE,"E4"),sQuery(id+"F0.wireOp",EDGE,"E5")])]}),"instanceName":"1"}),"instanceName":"1"});
            var Q18;
            Q18=makeQuery(id+"F5.opPattern","COPY",BODY,{"derivedFrom":makeQuery(id+"F1.opRevolve","SWEPT_BODY",BODY,{"disambiguationData":[OSD([sQuery(id+"F0.wireOp",EDGE,"E0"),sQuery(id+"F0.wireOp",EDGE,"E3"),sQuery(id+"F0.wireOp",EDGE,"E4"),sQuery(id+"F0.wireOp",EDGE,"E5")])]}),"instanceName":"1"});
            var Q19;
            Q19=makeQuery(id+"F7.opPattern","COPY",BODY,{"derivedFrom":makeQuery(id+"F1.opRevolve","SWEPT_BODY",BODY,{"disambiguationData":[OSD([sQuery(id+"F0.wireOp",EDGE,"E0"),sQuery(id+"F0.wireOp",EDGE,"E3"),sQuery(id+"F0.wireOp",EDGE,"E4"),sQuery(id+"F0.wireOp",EDGE,"E5")])]}),"instanceName":"1"});
            var Q20;
            Q20=makeQuery(id+"F1.opRevolve","SWEPT_BODY",BODY,{"disambiguationData":[OSD([sQuery(id+"F0.wireOp",EDGE,"E0"),sQuery(id+"F0.wireOp",EDGE,"E3"),sQuery(id+"F0.wireOp",EDGE,"E4"),sQuery(id+"F0.wireOp",EDGE,"E5")])]});
            var Q21;
            Q21=makeQuery(id+"F7.opPattern","COPY",BODY,{"derivedFrom":makeQuery(id+"F6.opPattern","COPY",BODY,{"derivedFrom":makeQuery(id+"F5.opPattern","COPY",BODY,{"derivedFrom":makeQuery(id+"F1.opRevolve","SWEPT_BODY",BODY,{"disambiguationData":[OSD([sQuery(id+"F0.wireOp",EDGE,"E0"),sQuery(id+"F0.wireOp",EDGE,"E3"),sQuery(id+"F0.wireOp",EDGE,"E4"),sQuery(id+"F0.wireOp",EDGE,"E5")])]}),"instanceName":"1"}),"instanceName":"1"}),"instanceName":"1"});
            var Q22;
            Q22=makeQuery(id+"F6.opPattern","COPY",BODY,{"derivedFrom":makeQuery(id+"F5.opPattern","COPY",BODY,{"derivedFrom":makeQuery(id+"F1.opRevolve","SWEPT_BODY",BODY,{"disambiguationData":[OSD([sQuery(id+"F0.wireOp",EDGE,"E0"),sQuery(id+"F0.wireOp",EDGE,"E3"),sQuery(id+"F0.wireOp",EDGE,"E4"),sQuery(id+"F0.wireOp",EDGE,"E5")])]}),"instanceName":"1"}),"instanceName":"1"});
            var Q23;
            Q23=makeQuery(id+"F7.opPattern","COPY",BODY,{"derivedFrom":makeQuery(id+"F6.opPattern","COPY",BODY,{"derivedFrom":makeQuery(id+"F1.opRevolve","SWEPT_BODY",BODY,{"disambiguationData":[OSD([sQuery(id+"F0.wireOp",EDGE,"E0"),sQuery(id+"F0.wireOp",EDGE,"E3"),sQuery(id+"F0.wireOp",EDGE,"E4"),sQuery(id+"F0.wireOp",EDGE,"E5")])]}),"instanceName":"1"}),"instanceName":"1"});
            var Q24;
            Q24=makeQuery(id+"F10.opPattern","COPY",BODY,{"derivedFrom":makeQuery(id+"F6.opPattern","COPY",BODY,{"derivedFrom":makeQuery(id+"F5.opPattern","COPY",BODY,{"derivedFrom":makeQuery(id+"F1.opRevolve","SWEPT_BODY",BODY,{"disambiguationData":[OSD([sQuery(id+"F0.wireOp",EDGE,"E0"),sQuery(id+"F0.wireOp",EDGE,"E3"),sQuery(id+"F0.wireOp",EDGE,"E4"),sQuery(id+"F0.wireOp",EDGE,"E5")])]}),"instanceName":"1"}),"instanceName":"1"}),"instanceName":"1"});
            var Q25;
            Q25=makeQuery(id+"F10.opPattern","COPY",BODY,{"derivedFrom":makeQuery(id+"F7.opPattern","COPY",BODY,{"derivedFrom":makeQuery(id+"F6.opPattern","COPY",BODY,{"derivedFrom":makeQuery(id+"F1.opRevolve","SWEPT_BODY",BODY,{"disambiguationData":[OSD([sQuery(id+"F0.wireOp",EDGE,"E0"),sQuery(id+"F0.wireOp",EDGE,"E3"),sQuery(id+"F0.wireOp",EDGE,"E4"),sQuery(id+"F0.wireOp",EDGE,"E5")])]}),"instanceName":"1"}),"instanceName":"1"}),"instanceName":"1"});
            var Q26;
            Q26=makeQuery(id+"F10.opPattern","COPY",BODY,{"derivedFrom":makeQuery(id+"F6.opPattern","COPY",BODY,{"derivedFrom":makeQuery(id+"F1.opRevolve","SWEPT_BODY",BODY,{"disambiguationData":[OSD([sQuery(id+"F0.wireOp",EDGE,"E0"),sQuery(id+"F0.wireOp",EDGE,"E3"),sQuery(id+"F0.wireOp",EDGE,"E4"),sQuery(id+"F0.wireOp",EDGE,"E5")])]}),"instanceName":"1"}),"instanceName":"1"});
            var Q27;
            Q27=makeQuery(id+"F10.opPattern","COPY",BODY,{"derivedFrom":makeQuery(id+"F7.opPattern","COPY",BODY,{"derivedFrom":makeQuery(id+"F5.opPattern","COPY",BODY,{"derivedFrom":makeQuery(id+"F1.opRevolve","SWEPT_BODY",BODY,{"disambiguationData":[OSD([sQuery(id+"F0.wireOp",EDGE,"E0"),sQuery(id+"F0.wireOp",EDGE,"E3"),sQuery(id+"F0.wireOp",EDGE,"E4"),sQuery(id+"F0.wireOp",EDGE,"E5")])]}),"instanceName":"1"}),"instanceName":"1"}),"instanceName":"1"});
            var Q28;
            Q28=makeQuery(id+"F10.opPattern","COPY",BODY,{"derivedFrom":makeQuery(id+"F5.opPattern","COPY",BODY,{"derivedFrom":makeQuery(id+"F1.opRevolve","SWEPT_BODY",BODY,{"disambiguationData":[OSD([sQuery(id+"F0.wireOp",EDGE,"E0"),sQuery(id+"F0.wireOp",EDGE,"E3"),sQuery(id+"F0.wireOp",EDGE,"E4"),sQuery(id+"F0.wireOp",EDGE,"E5")])]}),"instanceName":"1"}),"instanceName":"1"});
            var Q29;
            Q29=makeQuery(id+"F10.opPattern","COPY",BODY,{"derivedFrom":makeQuery(id+"F7.opPattern","COPY",BODY,{"derivedFrom":makeQuery(id+"F1.opRevolve","SWEPT_BODY",BODY,{"disambiguationData":[OSD([sQuery(id+"F0.wireOp",EDGE,"E0"),sQuery(id+"F0.wireOp",EDGE,"E3"),sQuery(id+"F0.wireOp",EDGE,"E4"),sQuery(id+"F0.wireOp",EDGE,"E5")])]}),"instanceName":"1"}),"instanceName":"1"});
            var Q30;
            Q30=makeQuery(id+"F10.opPattern","COPY",BODY,{"derivedFrom":makeQuery(id+"F1.opRevolve","SWEPT_BODY",BODY,{"disambiguationData":[OSD([sQuery(id+"F0.wireOp",EDGE,"E0"),sQuery(id+"F0.wireOp",EDGE,"E3"),sQuery(id+"F0.wireOp",EDGE,"E4"),sQuery(id+"F0.wireOp",EDGE,"E5")])]}),"instanceName":"1"});
            var Q31;
            Q31=makeQuery(id+"F10.opPattern","COPY",BODY,{"derivedFrom":makeQuery(id+"F7.opPattern","COPY",BODY,{"derivedFrom":makeQuery(id+"F6.opPattern","COPY",BODY,{"derivedFrom":makeQuery(id+"F5.opPattern","COPY",BODY,{"derivedFrom":makeQuery(id+"F1.opRevolve","SWEPT_BODY",BODY,{"disambiguationData":[OSD([sQuery(id+"F0.wireOp",EDGE,"E0"),sQuery(id+"F0.wireOp",EDGE,"E3"),sQuery(id+"F0.wireOp",EDGE,"E4"),sQuery(id+"F0.wireOp",EDGE,"E5")])]}),"instanceName":"1"}),"instanceName":"1"}),"instanceName":"1"}),"instanceName":"1"});
            var Q32;
            Q32=sQuery(id+"F3.wireOp",VERTEX,"E7.end");
            var Q33;
            Q33=sQuery(id+"F3.wireOp",VERTEX,"E56.end");
            transform(context, id + "F12", {"entities" : qUnion([Q0, Q1, Q2, Q3, Q4, Q5, Q6, Q7, Q8, Q9, Q10, Q11, Q12, Q13, Q14, Q15, Q16, Q17, Q18, Q19, Q20, Q21, Q22, Q23, Q24, Q25, Q26, Q27, Q28, Q29, Q30, Q31]), "transformType" : TransformType.TRANSLATION_ENTITY, "oppositeDirectionEntity" : false, "transformLine" : qUnion([Q32, Q33]), "makeCopy" : true});
        }
        {
            var Q0;
            Q0=makeQuery(id+"F7.opPattern","COPY",BODY,{"derivedFrom":makeQuery(id+"F1.opRevolve","SWEPT_BODY",BODY,{"disambiguationData":[OSD([sQuery(id+"F0.wireOp",EDGE,"E0"),sQuery(id+"F0.wireOp",EDGE,"E3"),sQuery(id+"F0.wireOp",EDGE,"E4"),sQuery(id+"F0.wireOp",EDGE,"E5")])]}),"instanceName":"1"});
            var Q1;
            Q1=makeQuery(id+"F1.opRevolve","SWEPT_BODY",BODY,{"disambiguationData":[OSD([sQuery(id+"F0.wireOp",EDGE,"E0"),sQuery(id+"F0.wireOp",EDGE,"E3"),sQuery(id+"F0.wireOp",EDGE,"E4"),sQuery(id+"F0.wireOp",EDGE,"E5")])]});
            var Q2;
            Q2=makeQuery(id+"F7.opPattern","COPY",BODY,{"derivedFrom":makeQuery(id+"F6.opPattern","COPY",BODY,{"derivedFrom":makeQuery(id+"F5.opPattern","COPY",BODY,{"derivedFrom":makeQuery(id+"F1.opRevolve","SWEPT_BODY",BODY,{"disambiguationData":[OSD([sQuery(id+"F0.wireOp",EDGE,"E0"),sQuery(id+"F0.wireOp",EDGE,"E3"),sQuery(id+"F0.wireOp",EDGE,"E4"),sQuery(id+"F0.wireOp",EDGE,"E5")])]}),"instanceName":"1"}),"instanceName":"1"}),"instanceName":"1"});
            var Q3;
            Q3=makeQuery(id+"F6.opPattern","COPY",BODY,{"derivedFrom":makeQuery(id+"F5.opPattern","COPY",BODY,{"derivedFrom":makeQuery(id+"F1.opRevolve","SWEPT_BODY",BODY,{"disambiguationData":[OSD([sQuery(id+"F0.wireOp",EDGE,"E0"),sQuery(id+"F0.wireOp",EDGE,"E3"),sQuery(id+"F0.wireOp",EDGE,"E4"),sQuery(id+"F0.wireOp",EDGE,"E5")])]}),"instanceName":"1"}),"instanceName":"1"});
            var Q4;
            Q4=makeQuery(id+"F7.opPattern","COPY",BODY,{"derivedFrom":makeQuery(id+"F6.opPattern","COPY",BODY,{"derivedFrom":makeQuery(id+"F1.opRevolve","SWEPT_BODY",BODY,{"disambiguationData":[OSD([sQuery(id+"F0.wireOp",EDGE,"E0"),sQuery(id+"F0.wireOp",EDGE,"E3"),sQuery(id+"F0.wireOp",EDGE,"E4"),sQuery(id+"F0.wireOp",EDGE,"E5")])]}),"instanceName":"1"}),"instanceName":"1"});
            var Q5;
            Q5=makeQuery(id+"F6.opPattern","COPY",BODY,{"derivedFrom":makeQuery(id+"F1.opRevolve","SWEPT_BODY",BODY,{"disambiguationData":[OSD([sQuery(id+"F0.wireOp",EDGE,"E0"),sQuery(id+"F0.wireOp",EDGE,"E3"),sQuery(id+"F0.wireOp",EDGE,"E4"),sQuery(id+"F0.wireOp",EDGE,"E5")])]}),"instanceName":"1"});
            var Q6;
            Q6=makeQuery(id+"F7.opPattern","COPY",BODY,{"derivedFrom":makeQuery(id+"F5.opPattern","COPY",BODY,{"derivedFrom":makeQuery(id+"F1.opRevolve","SWEPT_BODY",BODY,{"disambiguationData":[OSD([sQuery(id+"F0.wireOp",EDGE,"E0"),sQuery(id+"F0.wireOp",EDGE,"E3"),sQuery(id+"F0.wireOp",EDGE,"E4"),sQuery(id+"F0.wireOp",EDGE,"E5")])]}),"instanceName":"1"}),"instanceName":"1"});
            var Q7;
            Q7=makeQuery(id+"F5.opPattern","COPY",BODY,{"derivedFrom":makeQuery(id+"F1.opRevolve","SWEPT_BODY",BODY,{"disambiguationData":[OSD([sQuery(id+"F0.wireOp",EDGE,"E0"),sQuery(id+"F0.wireOp",EDGE,"E3"),sQuery(id+"F0.wireOp",EDGE,"E4"),sQuery(id+"F0.wireOp",EDGE,"E5")])]}),"instanceName":"1"});
            var Q8;
            Q8=makeQuery(id+"F10.opPattern","COPY",BODY,{"derivedFrom":makeQuery(id+"F6.opPattern","COPY",BODY,{"derivedFrom":makeQuery(id+"F1.opRevolve","SWEPT_BODY",BODY,{"disambiguationData":[OSD([sQuery(id+"F0.wireOp",EDGE,"E0"),sQuery(id+"F0.wireOp",EDGE,"E3"),sQuery(id+"F0.wireOp",EDGE,"E4"),sQuery(id+"F0.wireOp",EDGE,"E5")])]}),"instanceName":"1"}),"instanceName":"1"});
            var Q9;
            Q9=makeQuery(id+"F10.opPattern","COPY",BODY,{"derivedFrom":makeQuery(id+"F7.opPattern","COPY",BODY,{"derivedFrom":makeQuery(id+"F6.opPattern","COPY",BODY,{"derivedFrom":makeQuery(id+"F1.opRevolve","SWEPT_BODY",BODY,{"disambiguationData":[OSD([sQuery(id+"F0.wireOp",EDGE,"E0"),sQuery(id+"F0.wireOp",EDGE,"E3"),sQuery(id+"F0.wireOp",EDGE,"E4"),sQuery(id+"F0.wireOp",EDGE,"E5")])]}),"instanceName":"1"}),"instanceName":"1"}),"instanceName":"1"});
            var Q10;
            Q10=makeQuery(id+"F10.opPattern","COPY",BODY,{"derivedFrom":makeQuery(id+"F6.opPattern","COPY",BODY,{"derivedFrom":makeQuery(id+"F5.opPattern","COPY",BODY,{"derivedFrom":makeQuery(id+"F1.opRevolve","SWEPT_BODY",BODY,{"disambiguationData":[OSD([sQuery(id+"F0.wireOp",EDGE,"E0"),sQuery(id+"F0.wireOp",EDGE,"E3"),sQuery(id+"F0.wireOp",EDGE,"E4"),sQuery(id+"F0.wireOp",EDGE,"E5")])]}),"instanceName":"1"}),"instanceName":"1"}),"instanceName":"1"});
            var Q11;
            Q11=makeQuery(id+"F10.opPattern","COPY",BODY,{"derivedFrom":makeQuery(id+"F7.opPattern","COPY",BODY,{"derivedFrom":makeQuery(id+"F6.opPattern","COPY",BODY,{"derivedFrom":makeQuery(id+"F5.opPattern","COPY",BODY,{"derivedFrom":makeQuery(id+"F1.opRevolve","SWEPT_BODY",BODY,{"disambiguationData":[OSD([sQuery(id+"F0.wireOp",EDGE,"E0"),sQuery(id+"F0.wireOp",EDGE,"E3"),sQuery(id+"F0.wireOp",EDGE,"E4"),sQuery(id+"F0.wireOp",EDGE,"E5")])]}),"instanceName":"1"}),"instanceName":"1"}),"instanceName":"1"}),"instanceName":"1"});
            var Q12;
            Q12=makeQuery(id+"F10.opPattern","COPY",BODY,{"derivedFrom":makeQuery(id+"F1.opRevolve","SWEPT_BODY",BODY,{"disambiguationData":[OSD([sQuery(id+"F0.wireOp",EDGE,"E0"),sQuery(id+"F0.wireOp",EDGE,"E3"),sQuery(id+"F0.wireOp",EDGE,"E4"),sQuery(id+"F0.wireOp",EDGE,"E5")])]}),"instanceName":"1"});
            var Q13;
            Q13=makeQuery(id+"F10.opPattern","COPY",BODY,{"derivedFrom":makeQuery(id+"F7.opPattern","COPY",BODY,{"derivedFrom":makeQuery(id+"F1.opRevolve","SWEPT_BODY",BODY,{"disambiguationData":[OSD([sQuery(id+"F0.wireOp",EDGE,"E0"),sQuery(id+"F0.wireOp",EDGE,"E3"),sQuery(id+"F0.wireOp",EDGE,"E4"),sQuery(id+"F0.wireOp",EDGE,"E5")])]}),"instanceName":"1"}),"instanceName":"1"});
            var Q14;
            Q14=makeQuery(id+"F10.opPattern","COPY",BODY,{"derivedFrom":makeQuery(id+"F5.opPattern","COPY",BODY,{"derivedFrom":makeQuery(id+"F1.opRevolve","SWEPT_BODY",BODY,{"disambiguationData":[OSD([sQuery(id+"F0.wireOp",EDGE,"E0"),sQuery(id+"F0.wireOp",EDGE,"E3"),sQuery(id+"F0.wireOp",EDGE,"E4"),sQuery(id+"F0.wireOp",EDGE,"E5")])]}),"instanceName":"1"}),"instanceName":"1"});
            var Q15;
            Q15=makeQuery(id+"F10.opPattern","COPY",BODY,{"derivedFrom":makeQuery(id+"F7.opPattern","COPY",BODY,{"derivedFrom":makeQuery(id+"F5.opPattern","COPY",BODY,{"derivedFrom":makeQuery(id+"F1.opRevolve","SWEPT_BODY",BODY,{"disambiguationData":[OSD([sQuery(id+"F0.wireOp",EDGE,"E0"),sQuery(id+"F0.wireOp",EDGE,"E3"),sQuery(id+"F0.wireOp",EDGE,"E4"),sQuery(id+"F0.wireOp",EDGE,"E5")])]}),"instanceName":"1"}),"instanceName":"1"}),"instanceName":"1"});
            var Q16;
            Q16=sQuery(id+"F3.wireOp",VERTEX,"E19.end");
            var Q17;
            Q17=sQuery(id+"F3.wireOp",VERTEX,"E20.start");
            transform(context, id + "F13", {"entities" : qUnion([Q0, Q1, Q2, Q3, Q4, Q5, Q6, Q7, Q8, Q9, Q10, Q11, Q12, Q13, Q14, Q15]), "transformType" : TransformType.TRANSLATION_ENTITY, "oppositeDirectionEntity" : false, "transformLine" : qUnion([Q16, Q17]), "makeCopy" : true});
        }
    });
